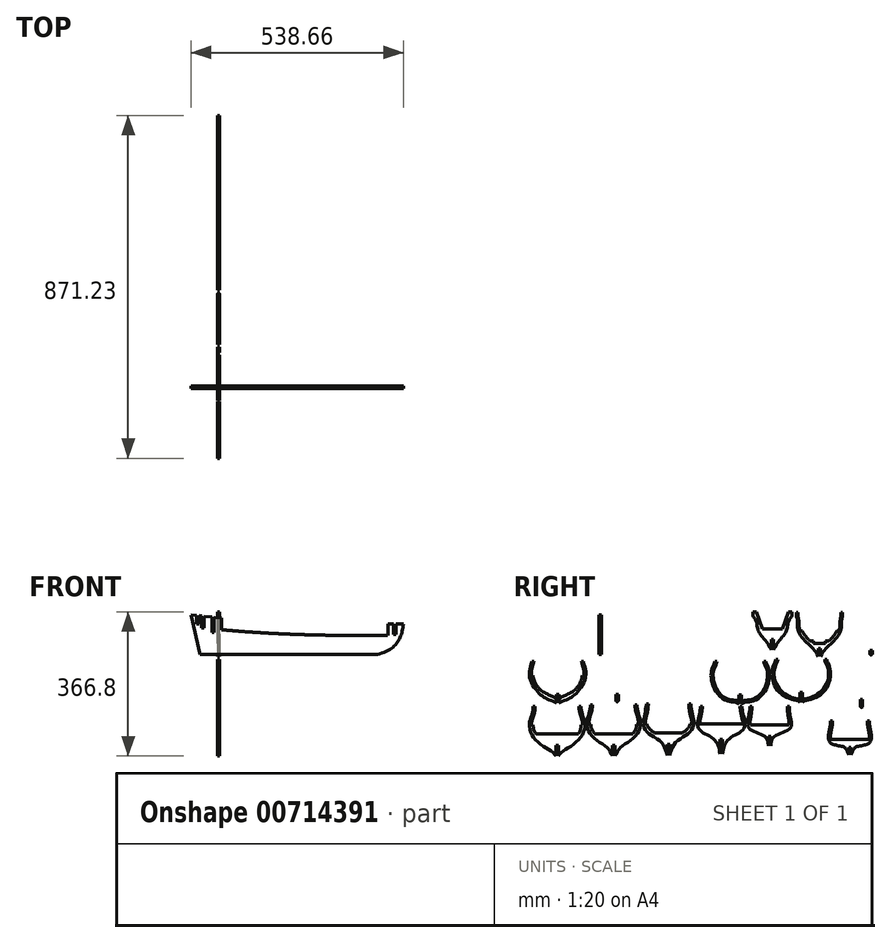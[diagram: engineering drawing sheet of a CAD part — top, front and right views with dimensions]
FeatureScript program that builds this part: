
annotation { "Feature Type Name" : "Feature", "Feature Type Description" : "" }
export const myFeature = defineFeature(function(context is Context, id is Id, definition is map)
    precondition{}
    {
        {
            var Q0;
            Q0=qCreatedBy(makeId("Right.planeOp"),FACE);
            var sketch = newSketch(context, id + "F0", { "sketchPlane" : qUnion([Q0])});
            skLineSegment(sketch, "E0", {"start": v(434.23, 36.76) * mm, "end": v(434.23, -63.24) * mm, "construction": true});
            skLineSegment(sketch, "E1", {"start": v(474.96, 36.76) * mm, "end": v(484.23, 36.76) * mm, "construction": true});
            skLineSegment(sketch, "E2", {"start": v(484.23, 36.76) * mm, "end": v(484.23, 26.76) * mm});
            skFitSpline(sketch, "E3", {"points": [v(484.23, 26.76) * mm, v(475.06, 12.03) * mm, v(469.54, -13) * mm, v(437.23, -60.52) * mm], "startDerivative": vector(-48.23, -63.75) * mm, "endDerivative": vector(-86.6, -185.01) * mm});
            skLineSegment(sketch, "E4", {"start": v(431.23, -33.48) * mm, "end": v(437.23, -33.48) * mm});
            skLineSegment(sketch, "E5", {"start": v(437.23, -33.48) * mm, "end": v(437.23, -60.52) * mm});
            skLineSegment(sketch, "E6.MirrorCS", {"start": v(437.23, -33.48) * mm, "end": v(431.23, -33.48) * mm});
            skFitSpline(sketch, "E7.MirrorCS", {"points": [v(384.23, 26.76) * mm, v(393.4, 12.03) * mm, v(398.93, -13) * mm, v(431.23, -60.52) * mm], "startDerivative": vector(48.23, -63.75) * mm, "endDerivative": vector(86.6, -185.01) * mm});
            skLineSegment(sketch, "E8.MirrorCS", {"start": v(393.5, 36.76) * mm, "end": v(384.23, 36.76) * mm, "construction": true});
            skLineSegment(sketch, "E9.MirrorCS", {"start": v(384.23, 36.76) * mm, "end": v(384.23, 26.76) * mm});
            skLineSegment(sketch, "E10.MirrorCS", {"start": v(431.23, -33.48) * mm, "end": v(431.23, -60.52) * mm});
            skLineSegment(sketch, "E11", {"start": v(384.23, 36.76) * mm, "end": v(393.5, 36.76) * mm});
            skLineSegment(sketch, "E12", {"start": v(434.23, -6.45) * mm, "end": v(459.23, -6.45) * mm});
            skLineSegment(sketch, "E13", {"start": v(459.23, -6.45) * mm, "end": v(474.96, 36.76) * mm});
            skLineSegment(sketch, "E14.MirrorCS", {"start": v(409.23, -6.45) * mm, "end": v(393.5, 36.76) * mm});
            skLineSegment(sketch, "E15.MirrorCS", {"start": v(434.23, -6.45) * mm, "end": v(409.23, -6.45) * mm});
            skPoint(sketch, "E16.orphan", {"position": v(434.23, 36.76) * mm});
            skLineSegment(sketch, "E17.trimOffspring", {"start": v(474.96, 36.76) * mm, "end": v(484.23, 36.76) * mm});
            skLineSegment(sketch, "E18", {"start": v(553.88, 36.76) * mm, "end": v(553.88, -78.24) * mm, "construction": true});
            skLineSegment(sketch, "E19", {"start": v(553.88, -56.43) * mm, "end": v(556.88, -56.43) * mm});
            skLineSegment(sketch, "E20", {"start": v(556.88, -56.43) * mm, "end": v(556.88, -76.43) * mm});
            skLineSegment(sketch, "E21", {"start": v(553.88, -43.08) * mm, "end": v(568.88, -43.08) * mm});
            skLineSegment(sketch, "E22", {"start": v(568.88, -43.08) * mm, "end": v(568.88, -37.08) * mm});
            skLineSegment(sketch, "E23", {"start": v(568.88, -37.08) * mm, "end": v(577.88, -37.08) * mm});
            skFitSpline(sketch, "E24", {"points": [v(577.88, -37.08) * mm, v(597.74, -12.04) * mm], "startDerivative": vector(24.58, 23.27) * mm, "endDerivative": vector(15.3, 31.89) * mm});
            skLineSegment(sketch, "E25", {"start": v(597.74, -12.04) * mm, "end": v(602.74, -12.04) * mm});
            skFitSpline(sketch, "E26", {"points": [v(602.74, -12.04) * mm, v(605.55, -2.16) * mm, v(606.03, 9.62) * mm, v(608.04, 23.19) * mm], "startDerivative": vector(9.73, 30.2) * mm, "endDerivative": vector(10.82, 49.21) * mm});
            skLineSegment(sketch, "E27", {"start": v(608.04, 23.19) * mm, "end": v(608.04, 35.69) * mm});
            skLineSegment(sketch, "E28", {"start": v(608.04, 35.69) * mm, "end": v(612.04, 35.69) * mm});
            skLineSegment(sketch, "E29", {"start": v(612.04, 35.69) * mm, "end": v(612.04, 23.19) * mm});
            skFitSpline(sketch, "E30", {"points": [v(612.04, 23.19) * mm, v(610.08, 13.13) * mm, v(606.58, -13.87) * mm, v(581.84, -45.86) * mm, v(556.88, -76.43) * mm], "startDerivative": vector(-26.95, -57.35) * mm, "endDerivative": vector(-67.73, -147.25) * mm});
            skLineSegment(sketch, "E31.MirrorCS", {"start": v(510, -12.04) * mm, "end": v(505, -12.04) * mm});
            skLineSegment(sketch, "E32.MirrorCS", {"start": v(538.88, -43.08) * mm, "end": v(538.88, -37.08) * mm});
            skLineSegment(sketch, "E33.MirrorCS", {"start": v(499.71, 35.69) * mm, "end": v(495.71, 35.69) * mm});
            skLineSegment(sketch, "E34.MirrorCS", {"start": v(538.88, -37.08) * mm, "end": v(529.88, -37.08) * mm});
            skLineSegment(sketch, "E35.MirrorCS", {"start": v(553.88, -56.43) * mm, "end": v(550.88, -56.43) * mm});
            skLineSegment(sketch, "E36.MirrorCS", {"start": v(499.71, 23.19) * mm, "end": v(499.71, 35.69) * mm});
            skLineSegment(sketch, "E37.MirrorCS", {"start": v(553.88, -43.08) * mm, "end": v(538.88, -43.08) * mm});
            skFitSpline(sketch, "E38.MirrorCS", {"points": [v(529.88, -37.08) * mm, v(510, -12.04) * mm], "startDerivative": vector(-24.58, 23.27) * mm, "endDerivative": vector(-15.3, 31.89) * mm});
            skFitSpline(sketch, "E39.MirrorCS", {"points": [v(495.71, 23.19) * mm, v(497.67, 13.13) * mm, v(501.17, -13.87) * mm, v(525.9, -45.86) * mm, v(550.88, -76.43) * mm], "startDerivative": vector(26.95, -57.35) * mm, "endDerivative": vector(67.73, -147.25) * mm});
            skLineSegment(sketch, "E40.MirrorCS", {"start": v(495.71, 35.69) * mm, "end": v(495.71, 23.19) * mm});
            skFitSpline(sketch, "E41.MirrorCS", {"points": [v(505, -12.04) * mm, v(502.2, -2.16) * mm, v(501.73, 9.62) * mm, v(499.71, 23.19) * mm], "startDerivative": vector(-9.73, 30.2) * mm, "endDerivative": vector(-10.82, 49.21) * mm});
            skLineSegment(sketch, "E42.MirrorCS", {"start": v(550.88, -56.43) * mm, "end": v(550.88, -76.43) * mm});
            skLineSegment(sketch, "E43", {"start": v(631.29, -238.47) * mm, "end": v(631.29, -331.47) * mm, "construction": true});
            skLineSegment(sketch, "E44", {"start": v(631.29, -307.47) * mm, "end": v(634.29, -307.47) * mm});
            skLineSegment(sketch, "E45", {"start": v(634.29, -307.47) * mm, "end": v(634.29, -327.47) * mm});
            skLineSegment(sketch, "E46", {"start": v(631.29, -287.47) * mm, "end": v(680.29, -287.47) * mm});
            skFitSpline(sketch, "E47", {"points": [v(680.29, -287.47) * mm, v(676.8, -255.54) * mm, v(675.93, -240.32) * mm], "startDerivative": vector(6.96, 57.92) * mm, "endDerivative": vector(0.97, 34.08) * mm});
            skLineSegment(sketch, "E48", {"start": v(675.93, -240.32) * mm, "end": v(680.93, -240.32) * mm});
            skFitSpline(sketch, "E49.0", {"points": [v(685.26, -287.9) * mm, v(685.58, -285.19) * mm, v(685.74, -279.83) * mm, v(685.13, -273.43) * mm, v(684.4, -268.56) * mm, v(683.76, -265.07) * mm, v(683.1, -261.75) * mm, v(682.48, -258.64) * mm, v(682.02, -256.25) * mm, v(681.72, -254.48) * mm, v(681.46, -252.8) * mm, v(681.21, -250.8) * mm, v(681.02, -248.57) * mm, v(680.9, -246.45) * mm, v(680.85, -243.7) * mm, v(680.89, -241.67) * mm, v(680.93, -240.29) * mm]});
            skFitSpline(sketch, "E50", {"points": [v(685.28, -287.7) * mm, v(677.18, -298.82) * mm, v(646.16, -307.43) * mm, v(634.29, -327.47) * mm], "startDerivative": vector(-1.84, -29.1) * mm, "endDerivative": vector(-19.55, -69.03) * mm});
            skLineSegment(sketch, "E51.MirrorCS", {"start": v(631.29, -307.47) * mm, "end": v(628.29, -307.47) * mm});
            skLineSegment(sketch, "E52.MirrorCS", {"start": v(586.65, -240.32) * mm, "end": v(581.65, -240.32) * mm});
            skFitSpline(sketch, "E53.MirrorCS", {"points": [v(577.32, -287.9) * mm, v(577, -285.19) * mm, v(576.84, -279.83) * mm, v(577.44, -273.43) * mm, v(578.19, -268.56) * mm, v(578.82, -265.07) * mm, v(579.47, -261.75) * mm, v(580.1, -258.64) * mm, v(580.56, -256.25) * mm, v(580.86, -254.48) * mm, v(581.12, -252.8) * mm, v(581.36, -250.8) * mm, v(581.56, -248.57) * mm, v(581.67, -246.45) * mm, v(581.72, -243.7) * mm, v(581.69, -241.67) * mm, v(581.65, -240.29) * mm]});
            skLineSegment(sketch, "E54.MirrorCS", {"start": v(631.29, -287.47) * mm, "end": v(582.29, -287.47) * mm});
            skFitSpline(sketch, "E55.MirrorCS", {"points": [v(577.3, -287.7) * mm, v(585.4, -298.82) * mm, v(616.42, -307.43) * mm, v(628.29, -327.47) * mm], "startDerivative": vector(1.84, -29.1) * mm, "endDerivative": vector(19.55, -69.03) * mm});
            skLineSegment(sketch, "E56.MirrorCS", {"start": v(628.29, -307.47) * mm, "end": v(628.29, -327.47) * mm});
            skFitSpline(sketch, "E57.MirrorCS", {"points": [v(582.29, -287.47) * mm, v(585.78, -255.54) * mm, v(586.65, -240.32) * mm], "startDerivative": vector(-6.96, 57.92) * mm, "endDerivative": vector(-0.97, 34.08) * mm});
            skLineSegment(sketch, "E58", {"start": v(427.1, -199.94) * mm, "end": v(427.1, -292.94) * mm, "construction": true});
            skLineSegment(sketch, "E59", {"start": v(427.1, -280.2) * mm, "end": v(430.1, -280.2) * mm});
            skLineSegment(sketch, "E60", {"start": v(430.1, -280.2) * mm, "end": v(430.1, -303.67) * mm});
            skLineSegment(sketch, "E61", {"start": v(427.1, -250.2) * mm, "end": v(476.1, -250.2) * mm});
            skFitSpline(sketch, "E62", {"points": [v(476.1, -250.2) * mm, v(474.89, -230.87) * mm, v(471.92, -203.24) * mm], "startDerivative": vector(6.96, 57.92) * mm, "endDerivative": vector(0.97, 34.08) * mm});
            skLineSegment(sketch, "E63", {"start": v(471.92, -203.24) * mm, "end": v(476.92, -203.24) * mm});
            skFitSpline(sketch, "E64", {"points": [v(476.92, -203.24) * mm, v(480.45, -258.14) * mm, v(439.2, -280.1) * mm, v(430.1, -303.67) * mm], "startDerivative": vector(-10.38, -162.31) * mm, "endDerivative": vector(0, -73.72) * mm});
            skLineSegment(sketch, "E65.MirrorCS", {"start": v(382.27, -203.24) * mm, "end": v(377.27, -203.24) * mm});
            skLineSegment(sketch, "E66.MirrorCS", {"start": v(427.1, -280.2) * mm, "end": v(424.1, -280.2) * mm});
            skLineSegment(sketch, "E67.MirrorCS", {"start": v(427.1, -250.2) * mm, "end": v(378.1, -250.2) * mm});
            skFitSpline(sketch, "E68.MirrorCS", {"points": [v(378.1, -250.2) * mm, v(379.3, -230.87) * mm, v(382.27, -203.24) * mm], "startDerivative": vector(-6.96, 57.92) * mm, "endDerivative": vector(-0.97, 34.08) * mm});
            skLineSegment(sketch, "E69.MirrorCS", {"start": v(424.1, -280.2) * mm, "end": v(424.1, -303.67) * mm});
            skFitSpline(sketch, "E70.MirrorCS", {"points": [v(377.27, -203.24) * mm, v(373.73, -258.14) * mm, v(414.98, -280.1) * mm, v(424.1, -303.67) * mm], "startDerivative": vector(10.38, -162.31) * mm, "endDerivative": vector(0, -73.72) * mm});
            skLineSegment(sketch, "E71", {"start": v(304.35, -200.68) * mm, "end": v(304.35, -328.26) * mm, "construction": true});
            skLineSegment(sketch, "E72", {"start": v(304.35, -286.93) * mm, "end": v(307.35, -286.93) * mm});
            skLineSegment(sketch, "E73", {"start": v(307.35, -286.93) * mm, "end": v(307.35, -323.93) * mm});
            skFitSpline(sketch, "E74", {"points": [v(307.35, -323.93) * mm, v(322.57, -287.38) * mm, v(361.1, -261.15) * mm, v(359.82, -224.14) * mm], "startDerivative": vector(21.91, 123.1) * mm, "endDerivative": vector(-38.34, 125.11) * mm});
            skFitSpline(sketch, "E75", {"points": [v(359.82, -224.14) * mm, v(356.94, -203.59) * mm], "startDerivative": vector(-4.9, 19.8) * mm, "endDerivative": vector(-2.83, 20.59) * mm});
            skLineSegment(sketch, "E76", {"start": v(356.94, -203.59) * mm, "end": v(351.94, -203.59) * mm});
            skFitSpline(sketch, "E77", {"points": [v(351.94, -203.59) * mm, v(355.32, -226.1) * mm, v(359.16, -248.74) * mm], "startDerivative": vector(7.99, -76.81) * mm, "endDerivative": vector(-4.81, -31.55) * mm});
            skLineSegment(sketch, "E78", {"start": v(359.16, -248.74) * mm, "end": v(304.35, -248.74) * mm});
            skLineSegment(sketch, "E79.MirrorCS", {"start": v(304.35, -286.93) * mm, "end": v(301.35, -286.93) * mm});
            skLineSegment(sketch, "E80.MirrorCS", {"start": v(249.54, -248.74) * mm, "end": v(304.35, -248.74) * mm});
            skFitSpline(sketch, "E81.MirrorCS", {"points": [v(256.77, -203.59) * mm, v(253.39, -226.1) * mm, v(249.54, -248.74) * mm], "startDerivative": vector(-7.99, -76.81) * mm, "endDerivative": vector(4.81, -31.55) * mm});
            skFitSpline(sketch, "E82.MirrorCS", {"points": [v(248.89, -224.14) * mm, v(251.77, -203.59) * mm], "startDerivative": vector(4.9, 19.8) * mm, "endDerivative": vector(2.83, 20.59) * mm});
            skLineSegment(sketch, "E83.MirrorCS", {"start": v(251.77, -203.59) * mm, "end": v(256.77, -203.59) * mm});
            skLineSegment(sketch, "E84.MirrorCS", {"start": v(301.35, -286.93) * mm, "end": v(301.35, -323.93) * mm});
            skFitSpline(sketch, "E85.MirrorCS", {"points": [v(301.35, -323.93) * mm, v(286.14, -287.38) * mm, v(247.6, -261.15) * mm, v(248.89, -224.14) * mm], "startDerivative": vector(-21.91, 123.1) * mm, "endDerivative": vector(38.34, 125.11) * mm});
            skLineSegment(sketch, "E86", {"start": v(170.41, -197.14) * mm, "end": v(170.41, -329.52) * mm, "construction": true});
            skLineSegment(sketch, "E87", {"start": v(170.41, -300.4) * mm, "end": v(173.41, -300.4) * mm});
            skLineSegment(sketch, "E88", {"start": v(173.41, -300.4) * mm, "end": v(173.41, -327.9) * mm});
            skFitSpline(sketch, "E89", {"points": [v(173.41, -327.9) * mm, v(188.1, -295.59) * mm, v(221.3, -271.7) * mm, v(234.8, -248.5) * mm, v(231.3, -227.53) * mm, v(226.84, -197.94) * mm], "startDerivative": vector(45.22, 164.82) * mm, "endDerivative": vector(-18.15, 163.37) * mm});
            skLineSegment(sketch, "E90", {"start": v(226.84, -197.94) * mm, "end": v(221.84, -197.94) * mm});
            skFitSpline(sketch, "E91", {"points": [v(221.84, -197.94) * mm, v(224.92, -222.59) * mm, v(229.57, -245.81) * mm, v(223.41, -262.16) * mm], "startDerivative": vector(5.07, -69.05) * mm, "endDerivative": vector(-26.5, -52.4) * mm});
            skLineSegment(sketch, "E92", {"start": v(205.06, -271.4) * mm, "end": v(170.41, -271.4) * mm});
            skLineSegment(sketch, "E93", {"start": v(229.37, -247.6) * mm, "end": v(225.37, -247.6) * mm});
            skFitSpline(sketch, "E94", {"points": [v(225.37, -247.6) * mm, v(205.06, -271.4) * mm], "startDerivative": vector(-6.96, -33.33) * mm, "endDerivative": vector(-27.82, -17.37) * mm});
            skPoint(sketch, "E95.MirrorCS.end.orphan", {"position": v(170.41, -271.4) * mm});
            skLineSegment(sketch, "E96.MirrorCS", {"start": v(113.98, -197.94) * mm, "end": v(118.98, -197.94) * mm});
            skLineSegment(sketch, "E97.MirrorCS", {"start": v(111.46, -247.6) * mm, "end": v(115.46, -247.6) * mm});
            skFitSpline(sketch, "E98.MirrorCS", {"points": [v(115.46, -247.6) * mm, v(135.76, -271.4) * mm], "startDerivative": vector(6.96, -33.33) * mm, "endDerivative": vector(27.82, -17.37) * mm});
            skLineSegment(sketch, "E99.MirrorCS", {"start": v(170.41, -300.4) * mm, "end": v(167.41, -300.4) * mm});
            skLineSegment(sketch, "E100.MirrorCS", {"start": v(167.41, -300.4) * mm, "end": v(167.41, -327.9) * mm});
            skFitSpline(sketch, "E101.MirrorCS", {"points": [v(167.41, -327.9) * mm, v(152.72, -295.59) * mm, v(119.52, -271.7) * mm, v(106.03, -248.5) * mm, v(109.53, -227.53) * mm, v(113.98, -197.94) * mm], "startDerivative": vector(-45.22, 164.82) * mm, "endDerivative": vector(18.15, 163.37) * mm});
            skFitSpline(sketch, "E102.MirrorCS", {"points": [v(118.98, -197.94) * mm, v(115.9, -222.59) * mm, v(111.26, -245.81) * mm, v(117.41, -262.16) * mm], "startDerivative": vector(-5.07, -69.05) * mm, "endDerivative": vector(26.5, -52.4) * mm});
            skLineSegment(sketch, "E103.MirrorCS", {"start": v(135.76, -271.4) * mm, "end": v(170.41, -271.4) * mm});
            skLineSegment(sketch, "E104", {"start": v(31.21, -330.55) * mm, "end": v(31.21, -197.66) * mm, "construction": true});
            skLineSegment(sketch, "E105", {"start": v(31.21, -302.26) * mm, "end": v(34.21, -302.26) * mm});
            skLineSegment(sketch, "E106", {"start": v(34.21, -302.26) * mm, "end": v(34.21, -329.26) * mm});
            skLineSegment(sketch, "E107", {"start": v(31.21, -273.26) * mm, "end": v(79.56, -273.26) * mm});
            skFitSpline(sketch, "E108", {"points": [v(79.56, -273.26) * mm, v(89.54, -249.8) * mm], "startDerivative": vector(14.49, 20.05) * mm, "endDerivative": vector(2.55, 34.74) * mm});
            skLineSegment(sketch, "E109", {"start": v(89.54, -249.8) * mm, "end": v(94, -249.8) * mm});
            skFitSpline(sketch, "E110", {"points": [v(34.21, -329.26) * mm, v(50.47, -306.43) * mm, v(86.42, -278.69) * mm, v(99.58, -243.24) * mm, v(94.07, -222.41) * mm, v(90.4, -200.06) * mm], "startDerivative": vector(65.96, 123.7) * mm, "endDerivative": vector(4.47, 119.64) * mm});
            skLineSegment(sketch, "E111", {"start": v(90.4, -200.06) * mm, "end": v(85.4, -200.06) * mm});
            skFitSpline(sketch, "E112", {"points": [v(85.4, -200.06) * mm, v(89.3, -224.07) * mm, v(94, -249.8) * mm], "startDerivative": vector(-0.26, -49.5) * mm, "endDerivative": vector(-5.6, -59.38) * mm});
            skLineSegment(sketch, "E113.MirrorCS", {"start": v(31.21, -302.26) * mm, "end": v(28.21, -302.26) * mm});
            skLineSegment(sketch, "E114.MirrorCS", {"start": v(-27.12, -249.8) * mm, "end": v(-31.58, -249.8) * mm});
            skLineSegment(sketch, "E115.MirrorCS", {"start": v(-27.98, -200.06) * mm, "end": v(-22.98, -200.06) * mm});
            skFitSpline(sketch, "E116.MirrorCS", {"points": [v(-17.14, -273.26) * mm, v(-27.12, -249.8) * mm], "startDerivative": vector(-14.49, 20.05) * mm, "endDerivative": vector(-2.55, 34.74) * mm});
            skFitSpline(sketch, "E117.MirrorCS", {"points": [v(-22.98, -200.06) * mm, v(-26.88, -224.07) * mm, v(-31.58, -249.8) * mm], "startDerivative": vector(0.26, -49.5) * mm, "endDerivative": vector(5.6, -59.38) * mm});
            skLineSegment(sketch, "E118.MirrorCS", {"start": v(28.21, -302.26) * mm, "end": v(28.21, -329.26) * mm});
            skFitSpline(sketch, "E119.MirrorCS", {"points": [v(28.21, -329.26) * mm, v(11.96, -306.43) * mm, v(-24, -278.69) * mm, v(-37.16, -243.24) * mm, v(-31.65, -222.41) * mm, v(-27.98, -200.06) * mm], "startDerivative": vector(-65.96, 123.7) * mm, "endDerivative": vector(-4.47, 119.64) * mm});
            skLineSegment(sketch, "E120.MirrorCS", {"start": v(31.21, -273.26) * mm, "end": v(-17.14, -273.26) * mm});
            skLineSegment(sketch, "E121", {"start": v(-112.69, -331.84) * mm, "end": v(-112.69, -198.94) * mm, "construction": true});
            skLineSegment(sketch, "E122", {"start": v(-112.69, -303.04) * mm, "end": v(-109.69, -303.04) * mm});
            skLineSegment(sketch, "E123", {"start": v(-109.69, -303.04) * mm, "end": v(-109.69, -330.04) * mm});
            skLineSegment(sketch, "E124", {"start": v(-112.69, -274.04) * mm, "end": v(-59.17, -274.04) * mm});
            skFitSpline(sketch, "E125", {"points": [v(-59.17, -274.04) * mm, v(-51.62, -250.77) * mm], "startDerivative": vector(14.49, 20.05) * mm, "endDerivative": vector(2.55, 34.74) * mm});
            skLineSegment(sketch, "E126", {"start": v(-51.62, -250.77) * mm, "end": v(-47.62, -250.77) * mm});
            skFitSpline(sketch, "E127", {"points": [v(-109.69, -330.04) * mm, v(-88.39, -311.83) * mm, v(-52, -281.07) * mm, v(-42.34, -248.14) * mm, v(-48.65, -223.57) * mm, v(-52.03, -203.28) * mm], "startDerivative": vector(65.96, 123.7) * mm, "endDerivative": vector(4.47, 119.64) * mm});
            skLineSegment(sketch, "E128", {"start": v(-52.03, -203.28) * mm, "end": v(-57.03, -203.28) * mm});
            skFitSpline(sketch, "E129", {"points": [v(-57.03, -203.28) * mm, v(-53.27, -226.4) * mm, v(-47.62, -250.77) * mm], "startDerivative": vector(-0.26, -49.5) * mm, "endDerivative": vector(-1.18, -57.37) * mm});
            skLineSegment(sketch, "E130.MirrorCS", {"start": v(-173.35, -203.28) * mm, "end": v(-168.35, -203.28) * mm});
            skLineSegment(sketch, "E131.MirrorCS", {"start": v(-112.69, -303.04) * mm, "end": v(-115.69, -303.04) * mm});
            skLineSegment(sketch, "E132.MirrorCS", {"start": v(-173.76, -250.77) * mm, "end": v(-177.76, -250.77) * mm});
            skFitSpline(sketch, "E133.MirrorCS", {"points": [v(-166.21, -274.04) * mm, v(-173.76, -250.77) * mm], "startDerivative": vector(-14.49, 20.05) * mm, "endDerivative": vector(-2.55, 34.74) * mm});
            skFitSpline(sketch, "E134.MirrorCS", {"points": [v(-115.69, -330.04) * mm, v(-136.99, -311.83) * mm, v(-173.37, -281.07) * mm, v(-183.04, -248.14) * mm, v(-176.73, -223.57) * mm, v(-173.35, -203.28) * mm], "startDerivative": vector(-65.96, 123.7) * mm, "endDerivative": vector(-4.47, 119.64) * mm});
            skFitSpline(sketch, "E135.MirrorCS", {"points": [v(-168.35, -203.28) * mm, v(-172.1, -226.4) * mm, v(-177.76, -250.77) * mm], "startDerivative": vector(0.26, -49.5) * mm, "endDerivative": vector(1.18, -57.37) * mm});
            skLineSegment(sketch, "E136.MirrorCS", {"start": v(-115.69, -303.04) * mm, "end": v(-115.69, -330.04) * mm});
            skLineSegment(sketch, "E137.MirrorCS", {"start": v(-112.69, -274.04) * mm, "end": v(-166.21, -274.04) * mm});
            skLineSegment(sketch, "E138", {"start": v(660.6, -86.17) * mm, "end": v(660.6, -218.2) * mm, "construction": true});
            skLineSegment(sketch, "E139", {"start": v(660.6, -186.45) * mm, "end": v(663.6, -186.45) * mm});
            skLineSegment(sketch, "E140", {"start": v(660.6, -158.45) * mm, "end": v(719.89, -158.45) * mm});
            skLineSegment(sketch, "E141", {"start": v(663.6, -186.45) * mm, "end": v(663.6, -212.64) * mm});
            skFitSpline(sketch, "E142", {"points": [v(663.6, -212.64) * mm, v(683.93, -201.2) * mm, v(715.46, -181.17) * mm, v(733.68, -139.31) * mm, v(726.03, -107.08) * mm, v(723.1, -87.44) * mm], "startDerivative": vector(105.46, 87.45) * mm, "endDerivative": vector(0, 69.3) * mm});
            skLineSegment(sketch, "E143", {"start": v(723.1, -87.44) * mm, "end": v(718.1, -87.44) * mm});
            skLineSegment(sketch, "E144", {"start": v(724.52, -135.14) * mm, "end": v(728.52, -135.14) * mm});
            skPoint(sketch, "E145", {"position": v(728.52, -135.14) * mm});
            skFitSpline(sketch, "E146.trimOffspring", {"points": [v(657.89, -205.7) * mm, v(659.19, -204.63) * mm, v(661.82, -202.64) * mm, v(665.83, -200.08) * mm, v(669.88, -197.86) * mm, v(673.96, -195.85) * mm, v(677.41, -194.27) * mm, v(680.23, -193) * mm, v(683.09, -191.71) * mm, v(686.7, -190.05) * mm, v(691.07, -187.9) * mm, v(695.38, -185.53) * mm, v(699.57, -182.91) * mm, v(703.57, -180) * mm, v(706.7, -177.26) * mm, v(709.06, -174.89) * mm, v(710.77, -172.98) * mm, v(712.43, -170.93) * mm, v(714.55, -168.05) * mm, v(717.02, -164.2) * mm, v(719.58, -159.3) * mm, v(721.7, -154.26) * mm, v(723.3, -149.24) * mm, v(724.16, -145.19) * mm, v(724.56, -142.1) * mm, v(724.71, -139.89) * mm, v(724.72, -137.8) * mm, v(724.6, -135.71) * mm, v(724.34, -133.64) * mm, v(723.86, -130.85) * mm, v(722.99, -127.3) * mm, v(721.85, -123.6) * mm, v(720.83, -120.54) * mm, v(720.04, -118.17) * mm, v(719.23, -115.73) * mm, v(718.43, -113.2) * mm, v(717.67, -110.59) * mm, v(716.97, -107.88) * mm, v(716.37, -105.2) * mm, v(715.68, -101.68) * mm, v(715.03, -97.46) * mm, v(714.51, -92.89) * mm, v(714.22, -88.98) * mm, v(714.14, -86.94) * mm, v(714.12, -86.06) * mm]});
            skFitSpline(sketch, "E147.trimOffspring", {"points": [v(660.28, -207.29) * mm, v(662.7, -205.28) * mm, v(666.42, -202.73) * mm, v(671.56, -199.92) * mm, v(675.5, -197.98) * mm, v(678.9, -196.42) * mm, v(681.71, -195.16) * mm, v(684.58, -193.86) * mm, v(688.26, -192.17) * mm, v(692.75, -189.96) * mm, v(697.24, -187.5) * mm, v(701.65, -184.75) * mm, v(705.91, -181.64) * mm, v(709.28, -178.72) * mm, v(711.83, -176.15) * mm, v(713.67, -174.09) * mm, v(715.45, -171.9) * mm, v(717.72, -168.82) * mm, v(720.33, -164.72) * mm, v(723.06, -159.53) * mm, v(725.3, -154.18) * mm, v(727.02, -148.8) * mm, v(727.96, -144.41) * mm, v(728.4, -141.02) * mm, v(728.57, -138.56) * mm, v(728.59, -136.2) * mm, v(728.45, -133.87) * mm, v(728.17, -131.57) * mm, v(727.64, -128.52) * mm, v(726.72, -124.73) * mm, v(725.3, -120.14) * mm, v(723.98, -116.23) * mm, v(722.92, -113.02) * mm, v(722.14, -110.56) * mm, v(721.4, -108.05) * mm, v(720.73, -105.48) * mm, v(720.15, -102.91) * mm, v(719.49, -99.54) * mm, v(718.85, -95.47) * mm, v(718.34, -91.03) * mm, v(718.1, -87.87) * mm, v(718.02, -85.76) * mm, v(718, -84.85) * mm, v(718, -84.42) * mm]});
            skLineSegment(sketch, "E148", {"start": v(728.52, -135.14) * mm, "end": v(728.52, -135.14) * mm});
            skLineSegment(sketch, "E149", {"start": v(507.81, -69.62) * mm, "end": v(507.81, -203.28) * mm, "construction": true});
            skLineSegment(sketch, "E150", {"start": v(507.81, -167.59) * mm, "end": v(510.81, -167.59) * mm});
            skLineSegment(sketch, "E151", {"start": v(522.81, -141.59) * mm, "end": v(568.66, -141.59) * mm});
            skLineSegment(sketch, "E152", {"start": v(510.81, -167.59) * mm, "end": v(510.81, -193.19) * mm});
            skFitSpline(sketch, "E153", {"points": [v(510.81, -193.19) * mm, v(532.9, -185.75) * mm, v(565.02, -166.24) * mm, v(581.24, -131.9) * mm, v(578.8, -101.51) * mm, v(572.64, -83.99) * mm], "startDerivative": vector(105.46, 87.45) * mm, "endDerivative": vector(0, 69.3) * mm});
            skLineSegment(sketch, "E154", {"start": v(572.64, -83.99) * mm, "end": v(567.64, -83.99) * mm});
            skLineSegment(sketch, "E155", {"start": v(572.99, -117.3) * mm, "end": v(576.99, -117.3) * mm});
            skPoint(sketch, "E156", {"position": v(576.99, -117.3) * mm});
            skFitSpline(sketch, "E157.trimOffspring", {"points": [v(506.52, -189.15) * mm, v(507.82, -188.07) * mm, v(510.45, -186.08) * mm, v(514.47, -183.53) * mm, v(518.52, -181.3) * mm, v(522.6, -179.3) * mm, v(526.05, -177.72) * mm, v(528.86, -176.45) * mm, v(531.72, -175.16) * mm, v(535.34, -173.5) * mm, v(539.7, -171.34) * mm, v(544.01, -168.97) * mm, v(548.2, -166.35) * mm, v(552.2, -163.44) * mm, v(555.34, -160.7) * mm, v(557.7, -158.33) * mm, v(559.4, -156.42) * mm, v(561.07, -154.37) * mm, v(563.19, -151.5) * mm, v(565.65, -147.64) * mm, v(568.22, -142.74) * mm, v(570.33, -137.7) * mm, v(571.93, -132.68) * mm, v(572.8, -128.63) * mm, v(573.2, -125.55) * mm, v(573.35, -123.33) * mm, v(573.35, -121.24) * mm, v(573.23, -119.16) * mm, v(572.98, -117.08) * mm, v(572.5, -114.3) * mm, v(571.62, -110.75) * mm, v(570.48, -107.05) * mm, v(569.46, -103.98) * mm, v(568.67, -101.61) * mm, v(567.86, -99.17) * mm, v(567.07, -96.65) * mm, v(566.3, -94.03) * mm, v(565.6, -91.32) * mm, v(565, -88.64) * mm, v(564.32, -85.12) * mm, v(563.66, -80.9) * mm, v(563.15, -76.33) * mm, v(562.85, -72.42) * mm, v(562.77, -70.38) * mm, v(562.76, -69.5) * mm]});
            skFitSpline(sketch, "E158.trimOffspring", {"points": [v(507.62, -189.34) * mm, v(509, -188.2) * mm, v(511.85, -186.33) * mm, v(516.22, -184.53) * mm, v(520.49, -183.39) * mm, v(523.92, -182.7) * mm, v(526.6, -182.16) * mm, v(528.59, -181.73) * mm, v(530.55, -181.24) * mm, v(532.5, -180.66) * mm, v(534.5, -179.97) * mm, v(537.24, -178.9) * mm, v(540.74, -177.27) * mm, v(544.97, -174.93) * mm, v(549.15, -172.2) * mm, v(553.22, -169.15) * mm, v(557.08, -165.8) * mm, v(560.07, -162.79) * mm, v(562.29, -160.27) * mm, v(564.4, -157.68) * mm, v(566.84, -154.3) * mm, v(570.29, -148.7) * mm, v(573.71, -141.36) * mm, v(575.89, -133.86) * mm, v(576.84, -127.95) * mm, v(577.17, -123.54) * mm, v(577.16, -119.18) * mm, v(576.8, -114.89) * mm, v(576.25, -111.38) * mm, v(575.66, -108.63) * mm, v(575.14, -106.6) * mm, v(574.65, -104.93) * mm, v(574.23, -103.6) * mm, v(573.79, -102.3) * mm, v(573.18, -100.67) * mm, v(572.16, -98.07) * mm, v(570.81, -94.9) * mm, v(569.56, -91.86) * mm, v(568.7, -89.5) * mm, v(568.17, -87.75) * mm, v(567.77, -85.96) * mm, v(567.64, -84.67) * mm, v(567.64, -83.99) * mm]});
            skLineSegment(sketch, "E159", {"start": v(576.99, -117.3) * mm, "end": v(576.99, -117.3) * mm});
            skLineSegment(sketch, "E160.MirrorCS", {"start": v(596.7, -135.14) * mm, "end": v(592.7, -135.14) * mm});
            skLineSegment(sketch, "E161.MirrorCS", {"start": v(660.6, -186.45) * mm, "end": v(657.6, -186.45) * mm});
            skLineSegment(sketch, "E162.MirrorCS", {"start": v(598.12, -87.44) * mm, "end": v(603.12, -87.44) * mm});
            skPoint(sketch, "E163.MirrorP", {"position": v(592.7, -135.14) * mm});
            skLineSegment(sketch, "E164.MirrorCS", {"start": v(660.6, -158.45) * mm, "end": v(601.33, -158.45) * mm});
            skLineSegment(sketch, "E165.MirrorCS", {"start": v(657.6, -186.45) * mm, "end": v(657.6, -212.64) * mm});
            skFitSpline(sketch, "E166.MirrorCS", {"points": [v(657.6, -212.64) * mm, v(637.29, -201.2) * mm, v(605.76, -181.17) * mm, v(587.53, -139.31) * mm, v(595.18, -107.08) * mm, v(598.12, -87.44) * mm], "startDerivative": vector(-105.46, 87.45) * mm, "endDerivative": vector(0, 69.3) * mm});
            skLineSegment(sketch, "E167.MirrorCS", {"start": v(592.7, -135.14) * mm, "end": v(592.7, -135.14) * mm});
            skFitSpline(sketch, "E168.MirrorCS", {"points": [v(660.94, -207.29) * mm, v(658.52, -205.28) * mm, v(654.8, -202.73) * mm, v(649.66, -199.92) * mm, v(645.71, -197.98) * mm, v(642.31, -196.42) * mm, v(639.5, -195.16) * mm, v(636.63, -193.86) * mm, v(632.95, -192.17) * mm, v(628.46, -189.96) * mm, v(623.98, -187.5) * mm, v(619.57, -184.75) * mm, v(615.3, -181.64) * mm, v(611.94, -178.72) * mm, v(609.4, -176.15) * mm, v(607.55, -174.09) * mm, v(605.77, -171.9) * mm, v(603.5, -168.82) * mm, v(600.89, -164.72) * mm, v(598.16, -159.53) * mm, v(595.91, -154.18) * mm, v(594.2, -148.8) * mm, v(593.26, -144.41) * mm, v(592.82, -141.02) * mm, v(592.64, -138.56) * mm, v(592.63, -136.2) * mm, v(592.77, -133.87) * mm, v(593.05, -131.57) * mm, v(593.57, -128.52) * mm, v(594.5, -124.73) * mm, v(595.92, -120.14) * mm, v(597.24, -116.23) * mm, v(598.3, -113.02) * mm, v(599.08, -110.56) * mm, v(599.81, -108.05) * mm, v(600.49, -105.48) * mm, v(601.06, -102.91) * mm, v(601.73, -99.54) * mm, v(602.37, -95.47) * mm, v(602.88, -91.03) * mm, v(603.1, -87.87) * mm, v(603.2, -85.76) * mm, v(603.21, -84.85) * mm, v(603.21, -84.42) * mm]});
            skFitSpline(sketch, "E169.MirrorCS", {"points": [v(663.33, -205.7) * mm, v(662.03, -204.63) * mm, v(659.4, -202.64) * mm, v(655.38, -200.08) * mm, v(651.33, -197.86) * mm, v(647.25, -195.85) * mm, v(643.8, -194.27) * mm, v(640.99, -193) * mm, v(638.13, -191.71) * mm, v(634.51, -190.05) * mm, v(630.15, -187.9) * mm, v(625.84, -185.53) * mm, v(621.65, -182.91) * mm, v(617.64, -180) * mm, v(614.5, -177.26) * mm, v(612.15, -174.89) * mm, v(610.44, -172.98) * mm, v(608.78, -170.93) * mm, v(606.66, -168.05) * mm, v(604.2, -164.2) * mm, v(601.63, -159.3) * mm, v(599.52, -154.26) * mm, v(597.92, -149.24) * mm, v(597.06, -145.19) * mm, v(596.66, -142.1) * mm, v(596.5, -139.89) * mm, v(596.5, -137.8) * mm, v(596.62, -135.71) * mm, v(596.87, -133.64) * mm, v(597.36, -130.85) * mm, v(598.23, -127.3) * mm, v(599.37, -123.6) * mm, v(600.39, -120.54) * mm, v(601.18, -118.17) * mm, v(601.99, -115.73) * mm, v(602.78, -113.2) * mm, v(603.55, -110.59) * mm, v(604.25, -107.88) * mm, v(604.85, -105.2) * mm, v(605.53, -101.68) * mm, v(606.19, -97.46) * mm, v(606.7, -92.89) * mm, v(607, -88.98) * mm, v(607.08, -86.94) * mm, v(607.1, -86.06) * mm]});
            skLineSegment(sketch, "E170", {"start": v(606.26, -201.43) * mm, "end": v(606.26, -201.43) * mm});
            skLineSegment(sketch, "E171", {"start": v(352.85, -71.56) * mm, "end": v(352.85, -197.83) * mm, "construction": true});
            skLineSegment(sketch, "E172", {"start": v(352.85, -174.23) * mm, "end": v(355.85, -174.23) * mm});
            skLineSegment(sketch, "E173", {"start": v(352.85, -148.23) * mm, "end": v(412.48, -148.23) * mm});
            skLineSegment(sketch, "E174", {"start": v(355.85, -174.23) * mm, "end": v(355.85, -196.99) * mm});
            skFitSpline(sketch, "E175", {"points": [v(355.85, -196.99) * mm, v(383.56, -190.18) * mm, v(414.33, -167.23) * mm, v(426.7, -129.68) * mm, v(424.26, -106.62) * mm, v(417.56, -88.81) * mm], "startDerivative": vector(203.97, 94.33) * mm, "endDerivative": vector(0, 69.3) * mm});
            skLineSegment(sketch, "E176", {"start": v(417.56, -88.81) * mm, "end": v(412.56, -88.81) * mm});
            skLineSegment(sketch, "E177", {"start": v(418.01, -121.87) * mm, "end": v(422.01, -121.87) * mm});
            skPoint(sketch, "E178", {"position": v(422.01, -121.87) * mm});
            skFitSpline(sketch, "E179.trimOffspring", {"points": [v(351.5, -193.36) * mm, v(352.8, -192.29) * mm, v(355.43, -190.3) * mm, v(359.44, -187.74) * mm, v(363.49, -185.51) * mm, v(367.57, -183.51) * mm, v(371.02, -181.93) * mm, v(373.84, -180.66) * mm, v(376.7, -179.37) * mm, v(380.31, -177.7) * mm, v(384.68, -175.55) * mm, v(388.99, -173.19) * mm, v(393.18, -170.57) * mm, v(397.18, -167.65) * mm, v(400.31, -164.92) * mm, v(402.67, -162.55) * mm, v(404.38, -160.63) * mm, v(406.04, -158.59) * mm, v(408.16, -155.7) * mm, v(410.62, -151.85) * mm, v(413.19, -146.95) * mm, v(415.3, -141.92) * mm, v(416.9, -136.9) * mm, v(417.77, -132.84) * mm, v(418.17, -129.76) * mm, v(418.32, -127.55) * mm, v(418.33, -125.45) * mm, v(418.2, -123.37) * mm, v(417.95, -121.3) * mm, v(417.46, -118.5) * mm, v(416.6, -114.96) * mm, v(415.45, -111.27) * mm, v(414.44, -108.2) * mm, v(413.64, -105.83) * mm, v(412.84, -103.38) * mm, v(412.04, -100.86) * mm, v(411.27, -98.25) * mm, v(410.57, -95.53) * mm, v(409.97, -92.85) * mm, v(409.3, -89.34) * mm, v(408.64, -85.12) * mm, v(408.12, -80.54) * mm, v(407.82, -76.64) * mm, v(407.74, -74.6) * mm, v(407.73, -73.72) * mm]});
            skFitSpline(sketch, "E180.trimOffspring", {"points": [v(353.75, -192.45) * mm, v(356.02, -191.4) * mm, v(360.24, -189.71) * mm, v(365.77, -188.16) * mm, v(370.6, -187.32) * mm, v(374.78, -186.87) * mm, v(377.8, -186.56) * mm, v(380.04, -186.22) * mm, v(381.42, -185.94) * mm, v(382.52, -185.67) * mm, v(383.64, -185.35) * mm, v(385.1, -184.86) * mm, v(386.97, -184.11) * mm, v(388.9, -183.21) * mm, v(390.9, -182.17) * mm, v(393.6, -180.6) * mm, v(397, -178.3) * mm, v(401.02, -175.07) * mm, v(404.2, -172.04) * mm, v(406.57, -169.45) * mm, v(408.26, -167.43) * mm, v(409.84, -165.34) * mm, v(411.77, -162.48) * mm, v(413.92, -158.7) * mm, v(416.09, -153.95) * mm, v(417.87, -149.04) * mm, v(419.29, -144.09) * mm, v(420.38, -139.16) * mm, v(421.04, -135.17) * mm, v(421.43, -132.09) * mm, v(421.67, -129.84) * mm, v(421.85, -127.68) * mm, v(422, -124.93) * mm, v(422.05, -121.71) * mm, v(421.84, -118.11) * mm, v(421.44, -115.25) * mm, v(420.95, -112.97) * mm, v(420.51, -111.25) * mm, v(419.98, -109.52) * mm, v(419.15, -107.16) * mm, v(417.84, -104.01) * mm, v(416.1, -100.15) * mm, v(414.71, -97) * mm, v(413.77, -94.55) * mm, v(413.17, -92.73) * mm, v(412.71, -90.88) * mm, v(412.56, -89.54) * mm, v(412.56, -88.81) * mm]});
            skLineSegment(sketch, "E181", {"start": v(522.81, -141.59) * mm, "end": v(522.81, -148.59) * mm});
            skLineSegment(sketch, "E182", {"start": v(522.81, -148.59) * mm, "end": v(507.81, -148.59) * mm});
            skPoint(sketch, "E183.orphan", {"position": v(507.81, -141.59) * mm});
            skLineSegment(sketch, "E184.MirrorCS", {"start": v(442.64, -117.3) * mm, "end": v(438.64, -117.3) * mm});
            skLineSegment(sketch, "E185.MirrorCS", {"start": v(443, -83.99) * mm, "end": v(448, -83.99) * mm});
            skPoint(sketch, "E186.MirrorP", {"position": v(438.64, -117.3) * mm});
            skLineSegment(sketch, "E187.MirrorCS", {"start": v(492.81, -148.59) * mm, "end": v(507.81, -148.59) * mm});
            skLineSegment(sketch, "E188.MirrorCS", {"start": v(507.81, -167.59) * mm, "end": v(504.81, -167.59) * mm});
            skLineSegment(sketch, "E189.MirrorCS", {"start": v(492.81, -141.59) * mm, "end": v(492.81, -148.59) * mm});
            skLineSegment(sketch, "E190.MirrorCS", {"start": v(504.81, -167.59) * mm, "end": v(504.81, -193.19) * mm});
            skLineSegment(sketch, "E191.MirrorCS", {"start": v(492.81, -141.59) * mm, "end": v(446.97, -141.59) * mm});
            skFitSpline(sketch, "E192.MirrorCS", {"points": [v(509.1, -189.15) * mm, v(507.8, -188.07) * mm, v(505.17, -186.08) * mm, v(501.16, -183.53) * mm, v(497.11, -181.3) * mm, v(493.03, -179.3) * mm, v(489.58, -177.72) * mm, v(486.77, -176.45) * mm, v(483.9, -175.16) * mm, v(480.29, -173.5) * mm, v(475.93, -171.34) * mm, v(471.61, -168.97) * mm, v(467.42, -166.35) * mm, v(463.42, -163.44) * mm, v(460.29, -160.7) * mm, v(457.93, -158.33) * mm, v(456.22, -156.42) * mm, v(454.56, -154.37) * mm, v(452.44, -151.5) * mm, v(449.98, -147.64) * mm, v(447.41, -142.74) * mm, v(445.3, -137.7) * mm, v(443.7, -132.68) * mm, v(442.84, -128.63) * mm, v(442.44, -125.55) * mm, v(442.28, -123.33) * mm, v(442.28, -121.24) * mm, v(442.4, -119.16) * mm, v(442.65, -117.08) * mm, v(443.14, -114.3) * mm, v(444, -110.75) * mm, v(445.15, -107.05) * mm, v(446.16, -103.98) * mm, v(446.96, -101.61) * mm, v(447.77, -99.17) * mm, v(448.56, -96.65) * mm, v(449.33, -94.03) * mm, v(450.03, -91.32) * mm, v(450.63, -88.64) * mm, v(451.31, -85.12) * mm, v(451.96, -80.9) * mm, v(452.48, -76.33) * mm, v(452.78, -72.42) * mm, v(452.86, -70.38) * mm, v(452.87, -69.5) * mm]});
            skFitSpline(sketch, "E193.MirrorCS", {"points": [v(508, -189.34) * mm, v(506.64, -188.2) * mm, v(503.78, -186.33) * mm, v(499.41, -184.53) * mm, v(495.14, -183.39) * mm, v(491.7, -182.7) * mm, v(489.03, -182.16) * mm, v(487.04, -181.73) * mm, v(485.08, -181.24) * mm, v(483.13, -180.66) * mm, v(481.12, -179.97) * mm, v(478.39, -178.9) * mm, v(474.9, -177.27) * mm, v(470.66, -174.93) * mm, v(466.48, -172.2) * mm, v(462.41, -169.15) * mm, v(458.55, -165.8) * mm, v(455.56, -162.79) * mm, v(453.34, -160.27) * mm, v(451.22, -157.68) * mm, v(448.79, -154.3) * mm, v(445.34, -148.7) * mm, v(441.92, -141.36) * mm, v(439.74, -133.86) * mm, v(438.8, -127.95) * mm, v(438.45, -123.54) * mm, v(438.47, -119.18) * mm, v(438.82, -114.89) * mm, v(439.38, -111.38) * mm, v(439.97, -108.63) * mm, v(440.49, -106.6) * mm, v(440.97, -104.93) * mm, v(441.4, -103.6) * mm, v(441.84, -102.3) * mm, v(442.44, -100.67) * mm, v(443.47, -98.07) * mm, v(444.81, -94.9) * mm, v(446.07, -91.86) * mm, v(446.92, -89.5) * mm, v(447.46, -87.75) * mm, v(447.86, -85.96) * mm, v(448, -84.67) * mm, v(448, -83.99) * mm]});
            skLineSegment(sketch, "E194.MirrorCS", {"start": v(438.64, -117.3) * mm, "end": v(438.64, -117.3) * mm});
            skFitSpline(sketch, "E195.MirrorCS", {"points": [v(504.81, -193.19) * mm, v(482.72, -185.75) * mm, v(450.6, -166.24) * mm, v(434.39, -131.9) * mm, v(436.83, -101.51) * mm, v(443, -83.99) * mm], "startDerivative": vector(-105.46, 87.45) * mm, "endDerivative": vector(0, 69.3) * mm});
            skLineSegment(sketch, "E196", {"start": v(684.79, 49.16) * mm, "end": v(684.79, -84.42) * mm, "construction": true});
            skLineSegment(sketch, "E197", {"start": v(684.79, -61.42) * mm, "end": v(687.79, -61.42) * mm});
            skLineSegment(sketch, "E198", {"start": v(687.79, -61.42) * mm, "end": v(687.79, -82.2) * mm});
            skLineSegment(sketch, "E199", {"start": v(684.79, -36.92) * mm, "end": v(729.56, -36.92) * mm});
            skFitSpline(sketch, "E200", {"points": [v(687.79, -82.2) * mm, v(717.58, -60.3) * mm, v(746.76, -27.7) * mm, v(751.56, 2.85) * mm, v(748.15, 32) * mm], "startDerivative": vector(112.56, 79.93) * mm, "endDerivative": vector(4.41, 198.36) * mm});
            skLineSegment(sketch, "E201", {"start": v(748.15, 32) * mm, "end": v(743.15, 32) * mm});
            skFitSpline(sketch, "E202.trimOffspring", {"points": [v(684.91, -78.02) * mm, v(689.63, -74.68) * mm, v(696.72, -69.73) * mm, v(706.36, -62.66) * mm, v(713.71, -56.96) * mm, v(721.25, -50.71) * mm, v(728.49, -44) * mm, v(733.9, -38.1) * mm, v(737.65, -33.23) * mm, v(739.7, -30.15) * mm, v(741.13, -27.66) * mm, v(742.1, -25.8) * mm, v(742.98, -23.92) * mm, v(744, -21.39) * mm, v(745.07, -18.17) * mm, v(746, -14.28) * mm, v(746.6, -10.42) * mm, v(746.93, -6.63) * mm, v(746.98, -3.58) * mm, v(746.91, -1.23) * mm, v(746.8, 0.47) * mm, v(746.65, 2.12) * mm, v(746.45, 3.7) * mm, v(746.22, 5.25) * mm, v(745.85, 7.32) * mm, v(745.32, 10) * mm, v(744.64, 13.49) * mm, v(743.98, 17.4) * mm, v(743.29, 23.37) * mm, v(743.08, 28.85) * mm, v(743.17, 33.15) * mm]});
            skFitSpline(sketch, "E203.trimOffspring", {"points": [v(682.58, -74.87) * mm, v(684.94, -73.19) * mm, v(689.67, -69.86) * mm, v(696.77, -64.82) * mm, v(702.74, -60.44) * mm, v(707.56, -56.76) * mm, v(711.21, -53.88) * mm, v(714.9, -50.87) * mm, v(718.56, -47.75) * mm, v(722.12, -44.54) * mm, v(725.54, -41.24) * mm, v(728.76, -37.87) * mm, v(731.73, -34.45) * mm, v(734.38, -31) * mm, v(736.28, -28.12) * mm, v(737.61, -25.84) * mm, v(738.35, -24.42) * mm, v(738.9, -23.29) * mm, v(739.4, -22.15) * mm, v(740, -20.7) * mm, v(740.61, -18.95) * mm, v(741.34, -16.6) * mm, v(742.05, -13.61) * mm, v(742.61, -10.04) * mm, v(742.91, -6.53) * mm, v(742.96, -3.7) * mm, v(742.9, -1.52) * mm, v(742.8, 0.06) * mm, v(742.66, 1.57) * mm, v(742.47, 3.03) * mm, v(742.25, 4.48) * mm, v(741.9, 6.46) * mm, v(741.38, 9.1) * mm, v(740.68, 12.65) * mm, v(740, 16.74) * mm, v(739.45, 21.42) * mm, v(739.13, 26.8) * mm, v(739.1, 30.91) * mm, v(739.15, 33.13) * mm]});
            skLineSegment(sketch, "E204", {"start": v(742.07, -13.26) * mm, "end": v(746.13, -13.26) * mm});
            skLineSegment(sketch, "E205.MirrorCS", {"start": v(627.51, -13.26) * mm, "end": v(623.44, -13.26) * mm});
            skLineSegment(sketch, "E206.MirrorCS", {"start": v(684.79, -61.42) * mm, "end": v(681.79, -61.42) * mm});
            skLineSegment(sketch, "E207.MirrorCS", {"start": v(621.43, 32) * mm, "end": v(626.43, 32) * mm});
            skLineSegment(sketch, "E208.MirrorCS", {"start": v(646.48, -87.44) * mm, "end": v(651.48, -87.44) * mm});
            skFitSpline(sketch, "E209.MirrorCS", {"points": [v(681.79, -82.2) * mm, v(652, -60.3) * mm, v(622.82, -27.7) * mm, v(618.02, 2.85) * mm, v(621.43, 32) * mm], "startDerivative": vector(-112.56, 79.93) * mm, "endDerivative": vector(-4.41, 198.36) * mm});
            skFitSpline(sketch, "E210.MirrorCS", {"points": [v(687, -74.87) * mm, v(684.63, -73.19) * mm, v(679.9, -69.86) * mm, v(672.8, -64.82) * mm, v(666.84, -60.44) * mm, v(662.01, -56.76) * mm, v(658.36, -53.88) * mm, v(654.67, -50.87) * mm, v(651.02, -47.75) * mm, v(647.45, -44.54) * mm, v(644.03, -41.24) * mm, v(640.81, -37.87) * mm, v(637.85, -34.45) * mm, v(635.2, -31) * mm, v(633.3, -28.12) * mm, v(631.97, -25.84) * mm, v(631.22, -24.42) * mm, v(630.68, -23.29) * mm, v(630.17, -22.15) * mm, v(629.59, -20.7) * mm, v(628.96, -18.95) * mm, v(628.24, -16.6) * mm, v(627.53, -13.61) * mm, v(626.97, -10.04) * mm, v(626.67, -6.53) * mm, v(626.62, -3.7) * mm, v(626.68, -1.52) * mm, v(626.78, 0.06) * mm, v(626.92, 1.57) * mm, v(627.1, 3.03) * mm, v(627.33, 4.48) * mm, v(627.68, 6.46) * mm, v(628.2, 9.1) * mm, v(628.9, 12.65) * mm, v(629.57, 16.74) * mm, v(630.12, 21.42) * mm, v(630.45, 26.8) * mm, v(630.47, 30.91) * mm, v(630.42, 33.13) * mm]});
            skLineSegment(sketch, "E211.MirrorCS", {"start": v(681.79, -61.42) * mm, "end": v(681.79, -82.2) * mm});
            skLineSegment(sketch, "E212.MirrorCS", {"start": v(684.79, -36.92) * mm, "end": v(640.01, -36.92) * mm});
            skFitSpline(sketch, "E213.MirrorCS", {"points": [v(684.66, -78.02) * mm, v(679.95, -74.68) * mm, v(672.86, -69.73) * mm, v(663.22, -62.66) * mm, v(655.86, -56.96) * mm, v(648.33, -50.71) * mm, v(641.09, -44) * mm, v(635.67, -38.1) * mm, v(631.93, -33.23) * mm, v(629.88, -30.15) * mm, v(628.44, -27.66) * mm, v(627.47, -25.8) * mm, v(626.6, -23.92) * mm, v(625.57, -21.39) * mm, v(624.51, -18.17) * mm, v(623.58, -14.28) * mm, v(622.97, -10.42) * mm, v(622.65, -6.63) * mm, v(622.6, -3.58) * mm, v(622.67, -1.23) * mm, v(622.77, 0.47) * mm, v(622.92, 2.12) * mm, v(623.12, 3.7) * mm, v(623.36, 5.25) * mm, v(623.73, 7.32) * mm, v(624.26, 10) * mm, v(624.94, 13.49) * mm, v(625.6, 17.4) * mm, v(626.3, 23.37) * mm, v(626.5, 28.85) * mm, v(626.4, 33.15) * mm]});
            skPoint(sketch, "E214", {"position": v(352.85, -197.83) * mm});
            skLineSegment(sketch, "E215.MirrorCS", {"start": v(287.7, -121.87) * mm, "end": v(283.7, -121.87) * mm});
            skLineSegment(sketch, "E216.MirrorCS", {"start": v(352.85, -174.23) * mm, "end": v(349.85, -174.23) * mm});
            skLineSegment(sketch, "E217.MirrorCS", {"start": v(288.14, -88.81) * mm, "end": v(293.14, -88.81) * mm});
            skLineSegment(sketch, "E218.MirrorCS", {"start": v(352.85, -148.23) * mm, "end": v(293.22, -148.23) * mm});
            skFitSpline(sketch, "E219.MirrorCS", {"points": [v(351.95, -192.45) * mm, v(349.68, -191.4) * mm, v(345.46, -189.71) * mm, v(339.93, -188.16) * mm, v(335.1, -187.32) * mm, v(330.93, -186.87) * mm, v(327.9, -186.56) * mm, v(325.66, -186.22) * mm, v(324.29, -185.94) * mm, v(323.18, -185.67) * mm, v(322.07, -185.35) * mm, v(320.6, -184.86) * mm, v(318.73, -184.11) * mm, v(316.8, -183.21) * mm, v(314.8, -182.17) * mm, v(312.11, -180.6) * mm, v(308.7, -178.3) * mm, v(304.69, -175.07) * mm, v(301.51, -172.04) * mm, v(299.13, -169.45) * mm, v(297.44, -167.43) * mm, v(295.87, -165.34) * mm, v(293.93, -162.48) * mm, v(291.78, -158.7) * mm, v(289.61, -153.95) * mm, v(287.83, -149.04) * mm, v(286.41, -144.09) * mm, v(285.32, -139.16) * mm, v(284.66, -135.17) * mm, v(284.27, -132.09) * mm, v(284.03, -129.84) * mm, v(283.85, -127.68) * mm, v(283.7, -124.93) * mm, v(283.65, -121.71) * mm, v(283.86, -118.11) * mm, v(284.27, -115.25) * mm, v(284.75, -112.97) * mm, v(285.2, -111.25) * mm, v(285.72, -109.52) * mm, v(286.55, -107.16) * mm, v(287.86, -104.01) * mm, v(289.6, -100.15) * mm, v(290.99, -97) * mm, v(291.94, -94.55) * mm, v(292.54, -92.73) * mm, v(292.99, -90.88) * mm, v(293.14, -89.54) * mm, v(293.14, -88.81) * mm]});
            skFitSpline(sketch, "E220.MirrorCS", {"points": [v(349.85, -196.99) * mm, v(322.14, -190.18) * mm, v(291.38, -167.23) * mm, v(279, -129.68) * mm, v(281.44, -106.62) * mm, v(288.14, -88.81) * mm], "startDerivative": vector(-203.97, 94.33) * mm, "endDerivative": vector(0, 69.3) * mm});
            skPoint(sketch, "E221.MirrorP", {"position": v(283.7, -121.87) * mm});
            skFitSpline(sketch, "E222.MirrorCS", {"points": [v(354.2, -193.36) * mm, v(352.9, -192.29) * mm, v(350.28, -190.3) * mm, v(346.26, -187.74) * mm, v(342.21, -185.51) * mm, v(338.13, -183.51) * mm, v(334.68, -181.93) * mm, v(331.87, -180.66) * mm, v(329.01, -179.37) * mm, v(325.4, -177.7) * mm, v(321.03, -175.55) * mm, v(316.72, -173.19) * mm, v(312.53, -170.57) * mm, v(308.52, -167.65) * mm, v(305.39, -164.92) * mm, v(303.03, -162.55) * mm, v(301.32, -160.63) * mm, v(299.66, -158.59) * mm, v(297.54, -155.7) * mm, v(295.08, -151.85) * mm, v(292.51, -146.95) * mm, v(290.4, -141.92) * mm, v(288.8, -136.9) * mm, v(287.94, -132.84) * mm, v(287.54, -129.76) * mm, v(287.38, -127.55) * mm, v(287.38, -125.45) * mm, v(287.5, -123.37) * mm, v(287.75, -121.3) * mm, v(288.24, -118.5) * mm, v(289.1, -114.96) * mm, v(290.25, -111.27) * mm, v(291.27, -108.2) * mm, v(292.06, -105.83) * mm, v(292.87, -103.38) * mm, v(293.66, -100.86) * mm, v(294.43, -98.25) * mm, v(295.13, -95.53) * mm, v(295.73, -92.85) * mm, v(296.41, -89.34) * mm, v(297.07, -85.12) * mm, v(297.58, -80.54) * mm, v(297.88, -76.64) * mm, v(297.96, -74.6) * mm, v(297.97, -73.72) * mm]});
            skLineSegment(sketch, "E223.MirrorCS", {"start": v(349.85, -174.23) * mm, "end": v(349.85, -196.99) * mm});
            skLineSegment(sketch, "E224", {"start": v(194.13, -69.7) * mm, "end": v(194.13, -194.17) * mm, "construction": true});
            skLineSegment(sketch, "E225", {"start": v(194.13, -170.57) * mm, "end": v(197.13, -170.57) * mm});
            skLineSegment(sketch, "E226", {"start": v(194.13, -145.57) * mm, "end": v(256.12, -145.57) * mm});
            skLineSegment(sketch, "E227", {"start": v(197.13, -170.57) * mm, "end": v(197.13, -195.12) * mm});
            skFitSpline(sketch, "E228", {"points": [v(197.13, -195.12) * mm, v(225.74, -188.44) * mm, v(255.8, -166.24) * mm, v(269.74, -130.04) * mm, v(265.53, -104.75) * mm, v(259.6, -88.78) * mm], "startDerivative": vector(203.97, 94.33) * mm, "endDerivative": vector(0, 69.3) * mm});
            skLineSegment(sketch, "E229", {"start": v(259.6, -88.78) * mm, "end": v(254.6, -88.78) * mm});
            skLineSegment(sketch, "E230", {"start": v(260.87, -122.9) * mm, "end": v(264.87, -122.9) * mm});
            skPoint(sketch, "E231", {"position": v(264.87, -122.9) * mm});
            skFitSpline(sketch, "E232.trimOffspring", {"points": [v(194.17, -192.73) * mm, v(195.47, -191.65) * mm, v(198.1, -189.66) * mm, v(202.11, -187.1) * mm, v(206.16, -184.88) * mm, v(210.24, -182.87) * mm, v(213.7, -181.3) * mm, v(216.5, -180.02) * mm, v(219.36, -178.73) * mm, v(222.98, -177.07) * mm, v(227.35, -174.91) * mm, v(231.66, -172.55) * mm, v(235.85, -169.93) * mm, v(239.85, -167) * mm, v(242.99, -164.28) * mm, v(245.34, -161.9) * mm, v(247.05, -160) * mm, v(248.71, -157.95) * mm, v(250.83, -155.07) * mm, v(253.3, -151.21) * mm, v(255.86, -146.31) * mm, v(257.97, -141.28) * mm, v(259.57, -136.26) * mm, v(260.44, -132.2) * mm, v(260.84, -129.12) * mm, v(261, -126.9) * mm, v(261, -124.81) * mm, v(260.87, -122.73) * mm, v(260.62, -120.65) * mm, v(260.14, -117.87) * mm, v(259.27, -114.32) * mm, v(258.12, -110.63) * mm, v(257.1, -107.56) * mm, v(256.31, -105.19) * mm, v(255.5, -102.75) * mm, v(254.71, -100.22) * mm, v(253.95, -97.6) * mm, v(253.24, -94.9) * mm, v(252.64, -92.21) * mm, v(251.96, -88.7) * mm, v(251.3, -84.48) * mm, v(250.8, -79.9) * mm, v(250.5, -76) * mm, v(250.42, -73.96) * mm, v(250.4, -73.08) * mm]});
            skFitSpline(sketch, "E233.trimOffspring", {"points": [v(199.9, -191.1) * mm, v(202.11, -189.94) * mm, v(206.25, -188.05) * mm, v(211.7, -186.24) * mm, v(216.48, -185.18) * mm, v(220.63, -184.53) * mm, v(223.63, -184.08) * mm, v(225.86, -183.63) * mm, v(227.22, -183.3) * mm, v(228.31, -182.97) * mm, v(229.41, -182.6) * mm, v(230.86, -182.04) * mm, v(232.68, -181.2) * mm, v(234.57, -180.21) * mm, v(236.51, -179.08) * mm, v(239.13, -177.38) * mm, v(242.43, -174.92) * mm, v(246.29, -171.5) * mm, v(249.32, -168.34) * mm, v(251.57, -165.64) * mm, v(253.16, -163.54) * mm, v(254.64, -161.38) * mm, v(256.44, -158.43) * mm, v(258.4, -154.56) * mm, v(260.35, -149.7) * mm, v(261.9, -144.72) * mm, v(263.08, -139.7) * mm, v(263.94, -134.73) * mm, v(264.41, -130.71) * mm, v(264.66, -127.61) * mm, v(264.8, -125.36) * mm, v(264.87, -123.19) * mm, v(264.9, -120.44) * mm, v(264.8, -117.22) * mm, v(264.41, -113.64) * mm, v(263.87, -110.8) * mm, v(263.28, -108.54) * mm, v(262.76, -106.85) * mm, v(262.15, -105.14) * mm, v(261.2, -102.82) * mm, v(259.75, -99.74) * mm, v(257.83, -95.96) * mm, v(256.3, -92.88) * mm, v(255.24, -90.48) * mm, v(254.55, -88.7) * mm, v(254.01, -86.86) * mm, v(253.8, -85.53) * mm, v(253.76, -84.8) * mm]});
            skPoint(sketch, "E234", {"position": v(194.13, -194.17) * mm});
            skLineSegment(sketch, "E235.MirrorCS", {"start": v(127.4, -122.9) * mm, "end": v(123.4, -122.9) * mm});
            skLineSegment(sketch, "E236.MirrorCS", {"start": v(194.13, -170.57) * mm, "end": v(191.13, -170.57) * mm});
            skLineSegment(sketch, "E237.MirrorCS", {"start": v(128.65, -88.78) * mm, "end": v(133.65, -88.78) * mm});
            skLineSegment(sketch, "E238.MirrorCS", {"start": v(194.13, -145.57) * mm, "end": v(132.14, -145.57) * mm});
            skFitSpline(sketch, "E239.MirrorCS", {"points": [v(188.36, -191.1) * mm, v(186.14, -189.94) * mm, v(182, -188.05) * mm, v(176.56, -186.24) * mm, v(171.77, -185.18) * mm, v(167.62, -184.53) * mm, v(164.62, -184.08) * mm, v(162.4, -183.63) * mm, v(161.03, -183.3) * mm, v(159.94, -182.97) * mm, v(158.84, -182.6) * mm, v(157.4, -182.04) * mm, v(155.57, -181.2) * mm, v(153.68, -180.21) * mm, v(151.74, -179.08) * mm, v(149.12, -177.38) * mm, v(145.83, -174.92) * mm, v(141.97, -171.5) * mm, v(138.94, -168.34) * mm, v(136.68, -165.64) * mm, v(135.1, -163.54) * mm, v(133.62, -161.38) * mm, v(131.82, -158.43) * mm, v(129.85, -154.56) * mm, v(127.9, -149.7) * mm, v(126.36, -144.72) * mm, v(125.17, -139.7) * mm, v(124.32, -134.73) * mm, v(123.84, -130.71) * mm, v(123.6, -127.61) * mm, v(123.46, -125.36) * mm, v(123.39, -123.19) * mm, v(123.36, -120.44) * mm, v(123.47, -117.22) * mm, v(123.84, -113.64) * mm, v(124.39, -110.8) * mm, v(124.97, -108.54) * mm, v(125.5, -106.85) * mm, v(126.1, -105.14) * mm, v(127.05, -102.82) * mm, v(128.5, -99.74) * mm, v(130.43, -95.96) * mm, v(131.96, -92.88) * mm, v(133.02, -90.48) * mm, v(133.7, -88.7) * mm, v(134.24, -86.86) * mm, v(134.46, -85.53) * mm, v(134.5, -84.8) * mm]});
            skFitSpline(sketch, "E240.MirrorCS", {"points": [v(191.13, -195.12) * mm, v(162.51, -188.44) * mm, v(132.46, -166.24) * mm, v(118.52, -130.04) * mm, v(122.72, -104.75) * mm, v(128.65, -88.78) * mm], "startDerivative": vector(-203.97, 94.33) * mm, "endDerivative": vector(0, 69.3) * mm});
            skPoint(sketch, "E241.MirrorP", {"position": v(123.4, -122.9) * mm});
            skFitSpline(sketch, "E242.MirrorCS", {"points": [v(194.1, -192.73) * mm, v(192.79, -191.65) * mm, v(190.16, -189.66) * mm, v(186.14, -187.1) * mm, v(182.1, -184.88) * mm, v(178.01, -182.87) * mm, v(174.56, -181.3) * mm, v(171.75, -180.02) * mm, v(168.9, -178.73) * mm, v(165.27, -177.07) * mm, v(160.9, -174.91) * mm, v(156.6, -172.55) * mm, v(152.4, -169.93) * mm, v(148.4, -167) * mm, v(145.27, -164.28) * mm, v(142.91, -161.9) * mm, v(141.2, -160) * mm, v(139.55, -157.95) * mm, v(137.42, -155.07) * mm, v(134.96, -151.21) * mm, v(132.4, -146.31) * mm, v(130.28, -141.28) * mm, v(128.68, -136.26) * mm, v(127.82, -132.2) * mm, v(127.42, -129.12) * mm, v(127.26, -126.9) * mm, v(127.26, -124.81) * mm, v(127.38, -122.73) * mm, v(127.63, -120.65) * mm, v(128.12, -117.87) * mm, v(128.99, -114.32) * mm, v(130.13, -110.63) * mm, v(131.15, -107.56) * mm, v(131.94, -105.19) * mm, v(132.75, -102.75) * mm, v(133.54, -100.22) * mm, v(134.31, -97.6) * mm, v(135.01, -94.9) * mm, v(135.61, -92.21) * mm, v(136.3, -88.7) * mm, v(136.95, -84.48) * mm, v(137.46, -79.9) * mm, v(137.76, -76) * mm, v(137.84, -73.96) * mm, v(137.86, -73.08) * mm]});
            skLineSegment(sketch, "E243.MirrorCS", {"start": v(191.13, -170.57) * mm, "end": v(191.13, -195.12) * mm});
            skLineSegment(sketch, "E244", {"start": v(39.7, -71.56) * mm, "end": v(39.7, -196.83) * mm, "construction": true});
            skLineSegment(sketch, "E245", {"start": v(39.7, -173.5) * mm, "end": v(42.7, -173.5) * mm});
            skLineSegment(sketch, "E246", {"start": v(39.7, -149.2) * mm, "end": v(98.83, -149.2) * mm});
            skLineSegment(sketch, "E247", {"start": v(42.7, -173.5) * mm, "end": v(42.7, -196.99) * mm});
            skFitSpline(sketch, "E248", {"points": [v(42.7, -196.99) * mm, v(73.37, -186.77) * mm, v(102.27, -161.6) * mm, v(113.54, -129.68) * mm, v(111.1, -106.62) * mm, v(105.18, -90.65) * mm], "startDerivative": vector(203.97, 94.33) * mm, "endDerivative": vector(0, 69.3) * mm});
            skLineSegment(sketch, "E249", {"start": v(105.18, -90.65) * mm, "end": v(100.18, -90.65) * mm});
            skLineSegment(sketch, "E250", {"start": v(105.16, -126.1) * mm, "end": v(109.16, -126.1) * mm});
            skPoint(sketch, "E251", {"position": v(109.16, -126.1) * mm});
            skFitSpline(sketch, "E252.trimOffspring", {"points": [v(38.34, -193.36) * mm, v(39.64, -192.29) * mm, v(42.28, -190.3) * mm, v(46.29, -187.74) * mm, v(50.34, -185.51) * mm, v(54.42, -183.51) * mm, v(57.87, -181.93) * mm, v(60.68, -180.66) * mm, v(63.54, -179.37) * mm, v(67.16, -177.7) * mm, v(71.52, -175.55) * mm, v(75.83, -173.19) * mm, v(80.02, -170.57) * mm, v(84.03, -167.65) * mm, v(87.16, -164.92) * mm, v(89.52, -162.55) * mm, v(91.23, -160.63) * mm, v(92.89, -158.59) * mm, v(95, -155.7) * mm, v(97.47, -151.85) * mm, v(100.04, -146.95) * mm, v(102.15, -141.92) * mm, v(103.75, -136.9) * mm, v(104.61, -132.84) * mm, v(105.01, -129.76) * mm, v(105.17, -127.55) * mm, v(105.17, -125.45) * mm, v(105.05, -123.37) * mm, v(104.8, -121.3) * mm, v(104.31, -118.5) * mm, v(103.44, -114.96) * mm, v(102.3, -111.27) * mm, v(101.28, -108.2) * mm, v(100.5, -105.83) * mm, v(99.68, -103.38) * mm, v(98.89, -100.86) * mm, v(98.12, -98.25) * mm, v(97.42, -95.53) * mm, v(96.82, -92.85) * mm, v(96.14, -89.34) * mm, v(95.49, -85.12) * mm, v(94.97, -80.54) * mm, v(94.67, -76.64) * mm, v(94.6, -74.6) * mm, v(94.58, -73.72) * mm]});
            skFitSpline(sketch, "E253.trimOffspring", {"points": [v(41.16, -191.41) * mm, v(43.43, -190.36) * mm, v(47.64, -188.67) * mm, v(53.17, -187.1) * mm, v(58, -186.25) * mm, v(62.17, -185.8) * mm, v(65.2, -185.49) * mm, v(67.44, -185.14) * mm, v(68.81, -184.86) * mm, v(69.92, -184.59) * mm, v(71.03, -184.27) * mm, v(72.5, -183.77) * mm, v(74.36, -183.02) * mm, v(76.3, -182.12) * mm, v(78.28, -181.07) * mm, v(80.98, -179.49) * mm, v(84.38, -177.18) * mm, v(88.4, -173.95) * mm, v(91.57, -170.92) * mm, v(93.94, -168.33) * mm, v(95.62, -166.3) * mm, v(97.2, -164.21) * mm, v(99.13, -161.35) * mm, v(101.27, -157.57) * mm, v(103.43, -152.8) * mm, v(105.2, -147.9) * mm, v(106.61, -142.94) * mm, v(107.7, -138.01) * mm, v(108.35, -134.02) * mm, v(108.74, -130.94) * mm, v(108.97, -128.69) * mm, v(109.14, -126.52) * mm, v(109.3, -123.78) * mm, v(109.34, -120.56) * mm, v(109.12, -116.96) * mm, v(108.7, -114.1) * mm, v(108.22, -111.82) * mm, v(107.78, -110.1) * mm, v(107.25, -108.37) * mm, v(106.41, -106.02) * mm, v(105.1, -102.87) * mm, v(103.35, -99) * mm, v(101.96, -95.86) * mm, v(101, -93.41) * mm, v(100.4, -91.6) * mm, v(99.95, -89.74) * mm, v(99.8, -88.4) * mm, v(99.8, -87.68) * mm]});
            skLineSegment(sketch, "E254.MirrorCS", {"start": v(-25.77, -126.1) * mm, "end": v(-29.77, -126.1) * mm});
            skLineSegment(sketch, "E255.MirrorCS", {"start": v(39.7, -173.5) * mm, "end": v(36.7, -173.5) * mm});
            skLineSegment(sketch, "E256.MirrorCS", {"start": v(-25.78, -90.65) * mm, "end": v(-20.78, -90.65) * mm});
            skLineSegment(sketch, "E257.MirrorCS", {"start": v(39.7, -149.2) * mm, "end": v(-19.43, -149.2) * mm});
            skFitSpline(sketch, "E258.MirrorCS", {"points": [v(38.24, -191.41) * mm, v(35.97, -190.36) * mm, v(31.75, -188.67) * mm, v(26.23, -187.1) * mm, v(21.4, -186.25) * mm, v(17.22, -185.8) * mm, v(14.2, -185.49) * mm, v(11.96, -185.14) * mm, v(10.59, -184.86) * mm, v(9.48, -184.59) * mm, v(8.37, -184.27) * mm, v(6.9, -183.77) * mm, v(5.03, -183.02) * mm, v(3.1, -182.12) * mm, v(1.11, -181.07) * mm, v(-1.58, -179.49) * mm, v(-4.99, -177.18) * mm, v(-9, -173.95) * mm, v(-12.17, -170.92) * mm, v(-14.54, -168.33) * mm, v(-16.22, -166.3) * mm, v(-17.8, -164.21) * mm, v(-19.73, -161.35) * mm, v(-21.87, -157.57) * mm, v(-24.03, -152.8) * mm, v(-25.8, -147.9) * mm, v(-27.21, -142.94) * mm, v(-28.3, -138.01) * mm, v(-28.95, -134.02) * mm, v(-29.34, -130.94) * mm, v(-29.57, -128.69) * mm, v(-29.75, -126.52) * mm, v(-29.9, -123.78) * mm, v(-29.94, -120.56) * mm, v(-29.72, -116.96) * mm, v(-29.31, -114.1) * mm, v(-28.83, -111.82) * mm, v(-28.38, -110.1) * mm, v(-27.85, -108.37) * mm, v(-27.01, -106.02) * mm, v(-25.7, -102.87) * mm, v(-23.95, -99) * mm, v(-22.56, -95.86) * mm, v(-21.6, -93.41) * mm, v(-21, -91.6) * mm, v(-20.55, -89.74) * mm, v(-20.4, -88.4) * mm, v(-20.4, -87.68) * mm]});
            skFitSpline(sketch, "E259.MirrorCS", {"points": [v(36.7, -196.99) * mm, v(6.02, -186.77) * mm, v(-22.87, -161.6) * mm, v(-34.15, -129.68) * mm, v(-31.7, -106.62) * mm, v(-25.78, -90.65) * mm], "startDerivative": vector(-203.97, 94.33) * mm, "endDerivative": vector(0, 69.3) * mm});
            skPoint(sketch, "E260.MirrorP", {"position": v(-29.77, -126.1) * mm});
            skFitSpline(sketch, "E261.MirrorCS", {"points": [v(41.06, -193.36) * mm, v(39.76, -192.29) * mm, v(37.12, -190.3) * mm, v(33.11, -187.74) * mm, v(29.06, -185.51) * mm, v(24.98, -183.51) * mm, v(21.53, -181.93) * mm, v(18.71, -180.66) * mm, v(15.86, -179.37) * mm, v(12.24, -177.7) * mm, v(7.87, -175.55) * mm, v(3.56, -173.19) * mm, v(-0.63, -170.57) * mm, v(-4.63, -167.65) * mm, v(-7.76, -164.92) * mm, v(-10.12, -162.55) * mm, v(-11.83, -160.63) * mm, v(-13.49, -158.59) * mm, v(-15.61, -155.7) * mm, v(-18.07, -151.85) * mm, v(-20.64, -146.95) * mm, v(-22.75, -141.92) * mm, v(-24.35, -136.9) * mm, v(-25.22, -132.84) * mm, v(-25.62, -129.76) * mm, v(-25.77, -127.55) * mm, v(-25.78, -125.45) * mm, v(-25.65, -123.37) * mm, v(-25.4, -121.3) * mm, v(-24.91, -118.5) * mm, v(-24.04, -114.96) * mm, v(-22.9, -111.27) * mm, v(-21.89, -108.2) * mm, v(-21.1, -105.83) * mm, v(-20.29, -103.38) * mm, v(-19.49, -100.86) * mm, v(-18.72, -98.25) * mm, v(-18.02, -95.53) * mm, v(-17.42, -92.85) * mm, v(-16.74, -89.34) * mm, v(-16.09, -85.12) * mm, v(-15.57, -80.54) * mm, v(-15.27, -76.64) * mm, v(-15.2, -74.6) * mm, v(-15.18, -73.72) * mm]});
            skLineSegment(sketch, "E262.MirrorCS", {"start": v(36.7, -173.5) * mm, "end": v(36.7, -196.99) * mm});
            skLineSegment(sketch, "E263", {"start": v(-111.24, -69.7) * mm, "end": v(-111.24, -194.96) * mm, "construction": true});
            skLineSegment(sketch, "E264", {"start": v(-111.24, -172.6) * mm, "end": v(-108.24, -172.6) * mm});
            skLineSegment(sketch, "E265", {"start": v(-111.24, -148.6) * mm, "end": v(-56.95, -148.6) * mm});
            skLineSegment(sketch, "E266", {"start": v(-108.24, -172.6) * mm, "end": v(-108.24, -195.12) * mm});
            skFitSpline(sketch, "E267", {"points": [v(-108.24, -195.12) * mm, v(-77.72, -181.16) * mm, v(-55.49, -161.1) * mm, v(-39.06, -118.63) * mm, v(-45.76, -88.78) * mm], "startDerivative": vector(203.97, 94.33) * mm, "endDerivative": vector(0, 69.3) * mm});
            skLineSegment(sketch, "E268", {"start": v(-45.76, -88.78) * mm, "end": v(-50.76, -88.78) * mm});
            skLineSegment(sketch, "E269", {"start": v(-48.49, -125.55) * mm, "end": v(-44.49, -125.55) * mm});
            skPoint(sketch, "E270", {"position": v(-44.49, -125.55) * mm});
            skFitSpline(sketch, "E271.trimOffspring", {"points": [v(-115.08, -188.6) * mm, v(-113.78, -187.52) * mm, v(-111.14, -185.53) * mm, v(-107.13, -182.97) * mm, v(-103.08, -180.75) * mm, v(-99, -178.74) * mm, v(-95.55, -177.16) * mm, v(-92.73, -175.9) * mm, v(-89.88, -174.6) * mm, v(-86.26, -172.94) * mm, v(-81.9, -170.78) * mm, v(-77.58, -168.42) * mm, v(-73.4, -165.8) * mm, v(-69.4, -162.88) * mm, v(-66.26, -160.15) * mm, v(-63.9, -157.78) * mm, v(-62.2, -155.87) * mm, v(-60.53, -153.82) * mm, v(-58.4, -150.94) * mm, v(-55.95, -147.08) * mm, v(-53.38, -142.18) * mm, v(-51.27, -137.15) * mm, v(-49.67, -132.13) * mm, v(-48.8, -128.08) * mm, v(-48.4, -125) * mm, v(-48.25, -122.78) * mm, v(-48.24, -120.68) * mm, v(-48.37, -118.6) * mm, v(-48.62, -116.53) * mm, v(-49.1, -113.74) * mm, v(-49.98, -110.2) * mm, v(-51.12, -106.5) * mm, v(-52.13, -103.43) * mm, v(-52.93, -101.06) * mm, v(-53.73, -98.62) * mm, v(-54.53, -96.1) * mm, v(-55.3, -93.48) * mm, v(-56, -90.77) * mm, v(-56.6, -88.08) * mm, v(-57.28, -84.57) * mm, v(-57.93, -80.35) * mm, v(-58.45, -75.78) * mm, v(-58.75, -71.87) * mm, v(-58.83, -69.83) * mm, v(-58.84, -68.95) * mm]});
            skLineSegment(sketch, "E272.MirrorCS", {"start": v(-174, -125.55) * mm, "end": v(-178, -125.55) * mm});
            skLineSegment(sketch, "E273.MirrorCS", {"start": v(-111.24, -172.6) * mm, "end": v(-114.24, -172.6) * mm});
            skLineSegment(sketch, "E274.MirrorCS", {"start": v(-176.72, -88.78) * mm, "end": v(-171.72, -88.78) * mm});
            skLineSegment(sketch, "E275.MirrorCS", {"start": v(-111.24, -148.6) * mm, "end": v(-165.52, -148.6) * mm});
            skFitSpline(sketch, "E276.MirrorCS", {"points": [v(-114.24, -195.12) * mm, v(-144.76, -181.16) * mm, v(-166.99, -161.1) * mm, v(-183.41, -118.63) * mm, v(-176.72, -88.78) * mm], "startDerivative": vector(-203.97, 94.33) * mm, "endDerivative": vector(0, 69.3) * mm});
            skPoint(sketch, "E277.MirrorP", {"position": v(-178, -125.55) * mm});
            skFitSpline(sketch, "E278.MirrorCS", {"points": [v(-107.4, -188.6) * mm, v(-108.7, -187.52) * mm, v(-111.34, -185.53) * mm, v(-115.35, -182.97) * mm, v(-119.4, -180.75) * mm, v(-123.48, -178.74) * mm, v(-126.93, -177.16) * mm, v(-129.74, -175.9) * mm, v(-132.6, -174.6) * mm, v(-136.22, -172.94) * mm, v(-140.58, -170.78) * mm, v(-144.9, -168.42) * mm, v(-149.08, -165.8) * mm, v(-153.09, -162.88) * mm, v(-156.22, -160.15) * mm, v(-158.58, -157.78) * mm, v(-160.29, -155.87) * mm, v(-161.95, -153.82) * mm, v(-164.07, -150.94) * mm, v(-166.53, -147.08) * mm, v(-169.1, -142.18) * mm, v(-171.2, -137.15) * mm, v(-172.8, -132.13) * mm, v(-173.67, -128.08) * mm, v(-174.07, -125) * mm, v(-174.23, -122.78) * mm, v(-174.23, -120.68) * mm, v(-174.1, -118.6) * mm, v(-173.86, -116.53) * mm, v(-173.37, -113.74) * mm, v(-172.5, -110.2) * mm, v(-171.36, -106.5) * mm, v(-170.34, -103.43) * mm, v(-169.55, -101.06) * mm, v(-168.74, -98.62) * mm, v(-167.95, -96.1) * mm, v(-167.18, -93.48) * mm, v(-166.48, -90.77) * mm, v(-165.88, -88.08) * mm, v(-165.2, -84.57) * mm, v(-164.55, -80.35) * mm, v(-164.03, -75.78) * mm, v(-163.73, -71.87) * mm, v(-163.65, -69.83) * mm, v(-163.64, -68.95) * mm]});
            skLineSegment(sketch, "E279.MirrorCS", {"start": v(-114.24, -172.6) * mm, "end": v(-114.24, -195.12) * mm});
            skFitSpline(sketch, "E280", {"points": [v(-44.49, -125.55) * mm, v(-50.76, -88.78) * mm], "startDerivative": vector(5.5, 38.92) * mm, "endDerivative": vector(-6.27, 36.77) * mm});
            skFitSpline(sketch, "E281.MirrorCS", {"points": [v(-178, -125.55) * mm, v(-171.72, -88.78) * mm], "startDerivative": vector(-5.5, 38.92) * mm, "endDerivative": vector(6.27, 36.77) * mm});
            skSolve(sketch);
        }
        {
            var Q0;
            Q0=qCreatedBy(makeId("Front.planeOp"),FACE);
            var sketch = newSketch(context, id + "F1", { "sketchPlane" : qUnion([Q0])});
            skLineSegment(sketch, "E282", {"start": v(-52.76, 27.43) * mm, "end": v(-66.2, 28.76) * mm});
            skLineSegment(sketch, "E283", {"start": v(11.17, 21.07) * mm, "end": v(11.17, -8.93) * mm});
            skFitSpline(sketch, "E284", {"points": [v(11.17, -8.93) * mm, v(433.17, -23.97) * mm], "startDerivative": vector(483.4, -44.47) * mm, "endDerivative": vector(364.06, -0.9) * mm});
            skLineSegment(sketch, "E285", {"start": v(433.17, -23.97) * mm, "end": v(433.17, 6.03) * mm});
            skLineSegment(sketch, "E286", {"start": v(433.17, 6.03) * mm, "end": v(447.96, 6.03) * mm});
            skLineSegment(sketch, "E287", {"start": v(-44.4, -71.24) * mm, "end": v(-66.2, 28.76) * mm});
            skLineSegment(sketch, "E288", {"start": v(-52.76, 6.4) * mm, "end": v(-46.76, 6.4) * mm});
            skFitSpline(sketch, "E289", {"points": [v(472.46, 6.03) * mm, v(406.44, -71.25) * mm], "startDerivative": vector(-9.53, -105.37) * mm, "endDerivative": vector(-148.23, -30.56) * mm});
            skLineSegment(sketch, "E290", {"start": v(-44.4, -71.24) * mm, "end": v(406.44, -71.25) * mm});
            skLineSegment(sketch, "E291", {"start": v(-39.83, 26.14) * mm, "end": v(-39.83, -3.87) * mm});
            skLineSegment(sketch, "E292", {"start": v(-39.83, -3.87) * mm, "end": v(-33.83, -3.87) * mm});
            skLineSegment(sketch, "E293", {"start": v(-33.83, -3.87) * mm, "end": v(-33.83, 25.54) * mm});
            skLineSegment(sketch, "E294", {"start": v(-66.2, 28.76) * mm, "end": v(474.62, 28.76) * mm, "construction": true});
            skLineSegment(sketch, "E295", {"start": v(474.62, 28.76) * mm, "end": v(474.62, -71.73) * mm, "construction": true});
            skLineSegment(sketch, "E296", {"start": v(-66.2, -70.56) * mm, "end": v(-66.2, 28.76) * mm, "construction": true});
            skLineSegment(sketch, "E297.trimOffspring", {"start": v(-13.78, 23.55) * mm, "end": v(-33.83, 25.54) * mm});
            skLineSegment(sketch, "E298", {"start": v(-46.76, 6.4) * mm, "end": v(-46.76, 26.83) * mm});
            skLineSegment(sketch, "E299", {"start": v(-52.76, 6.4) * mm, "end": v(-52.76, 27.43) * mm});
            skLineSegment(sketch, "E300.trimOffspring", {"start": v(-39.83, 26.14) * mm, "end": v(-46.76, 26.83) * mm});
            skLineSegment(sketch, "E301", {"start": v(447.96, -20.87) * mm, "end": v(453.96, -20.87) * mm});
            skLineSegment(sketch, "E302", {"start": v(453.96, -20.87) * mm, "end": v(453.96, 6.03) * mm});
            skLineSegment(sketch, "E303", {"start": v(447.96, -20.87) * mm, "end": v(447.96, 6.03) * mm});
            skLineSegment(sketch, "E304.trimOffspring", {"start": v(453.96, 6.03) * mm, "end": v(472.46, 6.03) * mm});
            skLineSegment(sketch, "E305", {"start": v(427.17, -23.97) * mm, "end": v(427.17, -44.5) * mm});
            skLineSegment(sketch, "E306", {"start": v(427.17, -44.5) * mm, "end": v(421.17, -44.5) * mm});
            skLineSegment(sketch, "E307", {"start": v(421.17, -44.5) * mm, "end": v(421.17, -30.88) * mm});
            skLineSegment(sketch, "E308", {"start": v(-13.78, 23.55) * mm, "end": v(-13.78, -15.2) * mm});
            skLineSegment(sketch, "E309", {"start": v(-13.78, -15.2) * mm, "end": v(-7.78, -15.2) * mm});
            skLineSegment(sketch, "E310", {"start": v(-7.78, -15.2) * mm, "end": v(-7.78, 22.95) * mm});
            skLineSegment(sketch, "E311.trimOffspring", {"start": v(11.17, 21.07) * mm, "end": v(-7.78, 22.95) * mm});
            skLineSegment(sketch, "E312", {"start": v(421.17, -30.88) * mm, "end": v(399.17, -30.88) * mm});
            skLineSegment(sketch, "E313", {"start": v(399.17, -30.88) * mm, "end": v(399.17, -23.88) * mm});
            skLineSegment(sketch, "E314", {"start": v(389.84, -23.86) * mm, "end": v(389.84, -48.36) * mm});
            skLineSegment(sketch, "E315", {"start": v(389.84, -48.36) * mm, "end": v(383.84, -48.36) * mm});
            skLineSegment(sketch, "E316", {"start": v(383.84, -48.36) * mm, "end": v(383.84, -23.83) * mm});
            skLineSegment(sketch, "E317", {"start": v(23.77, -10.06) * mm, "end": v(23.77, -39.06) * mm});
            skLineSegment(sketch, "E318", {"start": v(23.77, -39.06) * mm, "end": v(29.77, -39.06) * mm});
            skLineSegment(sketch, "E319", {"start": v(29.77, -39.06) * mm, "end": v(29.77, -10.59) * mm});
            skLineSegment(sketch, "E320", {"start": v(62.99, -13.26) * mm, "end": v(62.99, -42.26) * mm});
            skLineSegment(sketch, "E321", {"start": v(62.99, -42.26) * mm, "end": v(68.99, -42.26) * mm});
            skLineSegment(sketch, "E322", {"start": v(68.99, -42.26) * mm, "end": v(68.99, -13.7) * mm});
            skLineSegment(sketch, "E323", {"start": v(100.73, -15.5) * mm, "end": v(100.73, -44.5) * mm});
            skLineSegment(sketch, "E324", {"start": v(100.73, -44.5) * mm, "end": v(106.73, -44.5) * mm});
            skLineSegment(sketch, "E325", {"start": v(106.73, -44.5) * mm, "end": v(106.73, -15.8) * mm});
            skLineSegment(sketch, "E326", {"start": v(139.7, -18.12) * mm, "end": v(139.7, -46.12) * mm});
            skLineSegment(sketch, "E327", {"start": v(139.7, -46.12) * mm, "end": v(145.7, -46.12) * mm});
            skLineSegment(sketch, "E328", {"start": v(145.7, -46.12) * mm, "end": v(145.7, -18.43) * mm});
            skLineSegment(sketch, "E329", {"start": v(154.38, -18.85) * mm, "end": v(154.38, -25.85) * mm});
            skLineSegment(sketch, "E330", {"start": v(183.72, -20.13) * mm, "end": v(183.72, -46.13) * mm});
            skLineSegment(sketch, "E331", {"start": v(183.72, -46.13) * mm, "end": v(177.72, -46.13) * mm});
            skLineSegment(sketch, "E332", {"start": v(177.72, -46.13) * mm, "end": v(177.72, -25.85) * mm});
            skLineSegment(sketch, "E333", {"start": v(154.38, -25.85) * mm, "end": v(177.72, -25.85) * mm});
            skLineSegment(sketch, "E334", {"start": v(223.07, -21.5) * mm, "end": v(223.07, -47.68) * mm});
            skLineSegment(sketch, "E335", {"start": v(223.07, -47.68) * mm, "end": v(229.07, -47.68) * mm});
            skLineSegment(sketch, "E336", {"start": v(229.07, -47.68) * mm, "end": v(229.07, -21.68) * mm});
            skLineSegment(sketch, "E337", {"start": v(268.66, -22.63) * mm, "end": v(268.66, -47.68) * mm});
            skLineSegment(sketch, "E338", {"start": v(268.66, -47.68) * mm, "end": v(274.66, -47.74) * mm});
            skLineSegment(sketch, "E339", {"start": v(274.66, -47.74) * mm, "end": v(274.66, -22.74) * mm});
            skLineSegment(sketch, "E340", {"start": v(427.17, -23.97) * mm, "end": v(433.17, -23.97) * mm});
            skLineSegment(sketch, "E341", {"start": v(307.12, -23.25) * mm, "end": v(307.12, -47.68) * mm});
            skLineSegment(sketch, "E342", {"start": v(307.12, -47.68) * mm, "end": v(313.12, -47.68) * mm});
            skLineSegment(sketch, "E343", {"start": v(313.12, -47.68) * mm, "end": v(313.12, -23.32) * mm});
            skLineSegment(sketch, "E344", {"start": v(344.77, -23.62) * mm, "end": v(344.77, -47.68) * mm});
            skLineSegment(sketch, "E345", {"start": v(344.77, -47.68) * mm, "end": v(350.77, -47.68) * mm});
            skLineSegment(sketch, "E346", {"start": v(350.77, -47.68) * mm, "end": v(350.77, -23.67) * mm});
            skSolve(sketch);
        }
        {
            var Q0;
            Q0=qSketchRegion(id+"F1",true);
            extrude(context, id + "F2", {"entities" : qUnion([Q0]), "depth" : 6 * mm, "offsetDistance" : 25 * mm});
        }
        {
            var Q0;
            Q0=makeQuery(id+"F0.imprint","IMPRINT",FACE,{"disambiguationData":[TD([[makeQuery(id+"F0.imprint","IMPRINT",EDGE,{"derivedFrom":sQuery(id+"F0.wireOp",EDGE,"E2")}),-1.0]])]});
            extrude(context, id + "F3", {"entities" : qUnion([Q0]), "depth" : 6 * mm, "offsetDistance" : 25 * mm});
        }
        {
            var Q0;
            Q0=qSketchRegion(id+"F0",true);
            extrude(context, id + "F4", {"entities" : qUnion([Q0]), "operationType" : NewBodyOperationType.ADD, "depth" : 6 * mm, "offsetDistance" : 25 * mm});
        }
    });
